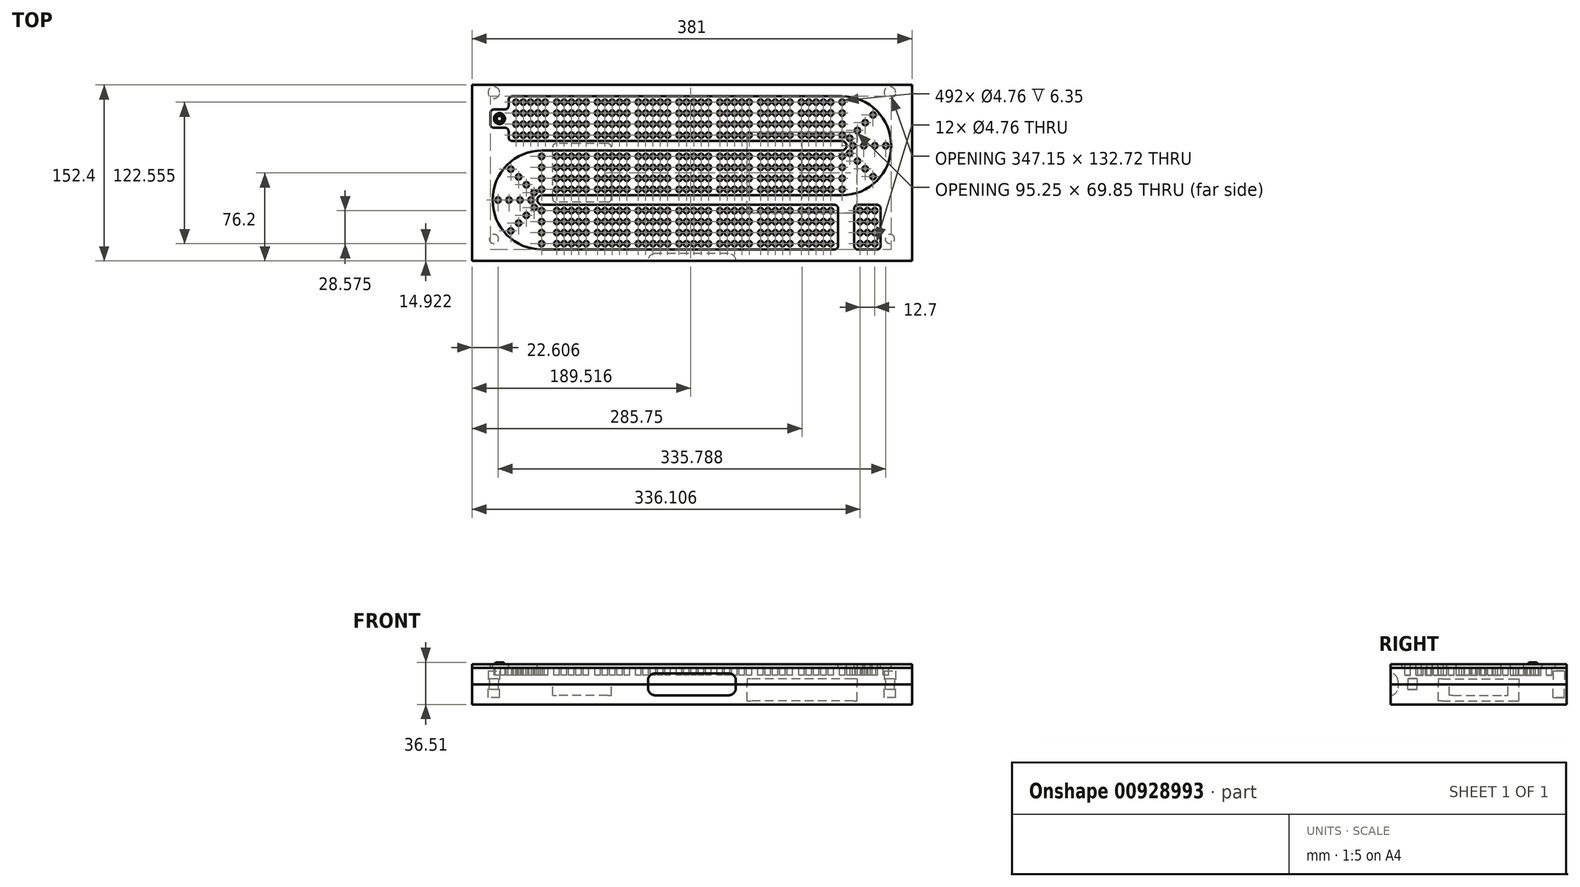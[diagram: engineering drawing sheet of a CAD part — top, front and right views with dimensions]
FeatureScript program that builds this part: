
annotation { "Feature Type Name" : "Feature", "Feature Type Description" : "" }
export const myFeature = defineFeature(function(context is Context, id is Id, definition is map)
    precondition{}
    {
        {
            var Q0;
            Q0=qCreatedBy(makeId("Top.planeOp"),FACE);
            var sketch = newSketch(context, id + "F0", { "sketchPlane" : qUnion([Q0])});
            skLineSegment(sketch, "E0.bottom", {"start": v(190.5, -76.2) * mm, "end": v(-190.5, -76.2) * mm});
            skLineSegment(sketch, "E0.top", {"start": v(190.5, 76.2) * mm, "end": v(-190.5, 76.2) * mm});
            skLineSegment(sketch, "E0.left", {"start": v(190.5, -76.2) * mm, "end": v(190.5, 76.2) * mm});
            skLineSegment(sketch, "E0.right", {"start": v(-190.5, -76.2) * mm, "end": v(-190.5, 76.2) * mm});
            skPoint(sketch, "E0.middle", {"position": v(0, 0) * mm});
            skSolve(sketch);
        }
        {
            var Q0;
            Q0=makeQuery(id+"F0.imprint","IMPRINT",FACE,{"disambiguationData":[TD([[makeQuery(id+"F0.imprint","IMPRINT",EDGE,{"derivedFrom":sQuery(id+"F0.wireOp",EDGE,"E0.bottom")}),-1.0]])]});
            extrude(context, id + "F1", {"entities" : qUnion([Q0]), "oppositeDirection" : true, "depth" : 17.46 * mm, "offsetDistance" : 25.4 * mm});
        }
        {
            var Q0;
            Q0=makeQuery(id+"F1.opExtrude","CAP_FACE",FACE,{"disambiguationData":[OSD([sQuery(id+"F0.wireOp",EDGE,"E0.bottom"),sQuery(id+"F0.wireOp",EDGE,"E0.top"),sQuery(id+"F0.wireOp",EDGE,"E0.left"),sQuery(id+"F0.wireOp",EDGE,"E0.right")])],"isStart":true});
            var sketch = newSketch(context, id + "F2", { "sketchPlane" : qUnion([Q0])});
            skCircle(sketch, "E1", {"center": v(1.59, -14.29) * mm, "radius": 2.38 * mm});
            skCircle(sketch, "E2.0.1.0", {"center": v(1.59, -4.76) * mm, "radius": 2.38 * mm});
            skCircle(sketch, "E2.0.2.0", {"center": v(1.59, 4.76) * mm, "radius": 2.38 * mm});
            skCircle(sketch, "E2.0.3.0", {"center": v(1.59, 14.29) * mm, "radius": 2.38 * mm});
            skCircle(sketch, "E2.1.0.0", {"center": v(7.94, -14.29) * mm, "radius": 2.38 * mm});
            skCircle(sketch, "E2.1.1.0", {"center": v(7.94, -4.76) * mm, "radius": 2.38 * mm});
            skCircle(sketch, "E2.1.2.0", {"center": v(7.94, 4.76) * mm, "radius": 2.38 * mm});
            skCircle(sketch, "E2.1.3.0", {"center": v(7.94, 14.29) * mm, "radius": 2.38 * mm});
            skCircle(sketch, "E2.2.0.0", {"center": v(14.29, -14.29) * mm, "radius": 2.38 * mm});
            skCircle(sketch, "E2.2.1.0", {"center": v(14.29, -4.76) * mm, "radius": 2.38 * mm});
            skCircle(sketch, "E2.2.2.0", {"center": v(14.29, 4.76) * mm, "radius": 2.38 * mm});
            skCircle(sketch, "E2.2.3.0", {"center": v(14.29, 14.29) * mm, "radius": 2.38 * mm});
            skCircle(sketch, "E3.1.0.0", {"center": v(-4.76, -14.29) * mm, "radius": 2.38 * mm});
            skCircle(sketch, "E3.2.0.0", {"center": v(-11.11, -14.29) * mm, "radius": 2.38 * mm});
            skCircle(sketch, "E4.0.1.0", {"center": v(-4.76, -4.76) * mm, "radius": 2.38 * mm});
            skCircle(sketch, "E4.0.2.0", {"center": v(-4.76, 4.76) * mm, "radius": 2.38 * mm});
            skCircle(sketch, "E4.0.3.0", {"center": v(-4.76, 14.29) * mm, "radius": 2.38 * mm});
            skCircle(sketch, "E5.0.1.0", {"center": v(-11.11, -4.76) * mm, "radius": 2.38 * mm});
            skCircle(sketch, "E5.0.2.0", {"center": v(-11.11, 4.76) * mm, "radius": 2.38 * mm});
            skCircle(sketch, "E5.0.3.0", {"center": v(-11.11, 14.29) * mm, "radius": 2.38 * mm});
            skCircle(sketch, "E6.1.0.0", {"center": v(30.54, 4.76) * mm, "radius": 2.38 * mm});
            skCircle(sketch, "E6.1.0.1", {"center": v(43.24, -14.29) * mm, "radius": 2.38 * mm});
            skCircle(sketch, "E6.1.0.2", {"center": v(43.24, -4.76) * mm, "radius": 2.38 * mm});
            skCircle(sketch, "E6.1.0.3", {"center": v(43.24, 14.29) * mm, "radius": 2.38 * mm});
            skCircle(sketch, "E6.1.0.4", {"center": v(49.6, 14.29) * mm, "radius": 2.38 * mm});
            skCircle(sketch, "E6.1.0.5", {"center": v(24.2, -14.29) * mm, "radius": 2.38 * mm});
            skCircle(sketch, "E6.1.0.6", {"center": v(30.54, -4.76) * mm, "radius": 2.38 * mm});
            skCircle(sketch, "E6.1.0.7", {"center": v(49.6, -4.76) * mm, "radius": 2.38 * mm});
            skCircle(sketch, "E6.1.0.8", {"center": v(36.9, 14.29) * mm, "radius": 2.38 * mm});
            skCircle(sketch, "E6.1.0.9", {"center": v(30.54, -14.29) * mm, "radius": 2.38 * mm});
            skCircle(sketch, "E6.1.0.10", {"center": v(24.2, -4.76) * mm, "radius": 2.38 * mm});
            skCircle(sketch, "E6.1.0.11", {"center": v(49.6, -14.29) * mm, "radius": 2.38 * mm});
            skCircle(sketch, "E6.1.0.12", {"center": v(36.9, -14.29) * mm, "radius": 2.38 * mm});
            skCircle(sketch, "E6.1.0.13", {"center": v(36.9, -4.76) * mm, "radius": 2.38 * mm});
            skCircle(sketch, "E6.1.0.14", {"center": v(30.54, 14.29) * mm, "radius": 2.38 * mm});
            skCircle(sketch, "E6.1.0.15", {"center": v(43.24, 4.76) * mm, "radius": 2.38 * mm});
            skCircle(sketch, "E6.1.0.16", {"center": v(24.2, 14.29) * mm, "radius": 2.38 * mm});
            skCircle(sketch, "E6.1.0.17", {"center": v(49.6, 4.76) * mm, "radius": 2.38 * mm});
            skCircle(sketch, "E6.1.0.18", {"center": v(24.2, 4.76) * mm, "radius": 2.38 * mm});
            skCircle(sketch, "E6.1.0.19", {"center": v(36.9, 4.76) * mm, "radius": 2.38 * mm});
            skCircle(sketch, "E6.2.0.0", {"center": v(65.85, 4.76) * mm, "radius": 2.38 * mm});
            skCircle(sketch, "E6.2.0.1", {"center": v(78.55, -14.29) * mm, "radius": 2.38 * mm});
            skCircle(sketch, "E6.2.0.2", {"center": v(78.55, -4.76) * mm, "radius": 2.38 * mm});
            skCircle(sketch, "E6.2.0.3", {"center": v(78.55, 14.29) * mm, "radius": 2.38 * mm});
            skCircle(sketch, "E6.2.0.4", {"center": v(84.9, 14.29) * mm, "radius": 2.38 * mm});
            skCircle(sketch, "E6.2.0.5", {"center": v(59.5, -14.29) * mm, "radius": 2.38 * mm});
            skCircle(sketch, "E6.2.0.6", {"center": v(65.85, -4.76) * mm, "radius": 2.38 * mm});
            skCircle(sketch, "E6.2.0.7", {"center": v(84.9, -4.76) * mm, "radius": 2.38 * mm});
            skCircle(sketch, "E6.2.0.8", {"center": v(72.2, 14.29) * mm, "radius": 2.38 * mm});
            skCircle(sketch, "E6.2.0.9", {"center": v(65.85, -14.29) * mm, "radius": 2.38 * mm});
            skCircle(sketch, "E6.2.0.10", {"center": v(59.5, -4.76) * mm, "radius": 2.38 * mm});
            skCircle(sketch, "E6.2.0.11", {"center": v(84.9, -14.29) * mm, "radius": 2.38 * mm});
            skCircle(sketch, "E6.2.0.12", {"center": v(72.2, -14.29) * mm, "radius": 2.38 * mm});
            skCircle(sketch, "E6.2.0.13", {"center": v(72.2, -4.76) * mm, "radius": 2.38 * mm});
            skCircle(sketch, "E6.2.0.14", {"center": v(65.85, 14.29) * mm, "radius": 2.38 * mm});
            skCircle(sketch, "E6.2.0.15", {"center": v(78.55, 4.76) * mm, "radius": 2.38 * mm});
            skCircle(sketch, "E6.2.0.16", {"center": v(59.5, 14.29) * mm, "radius": 2.38 * mm});
            skCircle(sketch, "E6.2.0.17", {"center": v(84.9, 4.76) * mm, "radius": 2.38 * mm});
            skCircle(sketch, "E6.2.0.18", {"center": v(59.5, 4.76) * mm, "radius": 2.38 * mm});
            skCircle(sketch, "E6.2.0.19", {"center": v(72.2, 4.76) * mm, "radius": 2.38 * mm});
            skCircle(sketch, "E6.3.0.0", {"center": v(101.16, 4.76) * mm, "radius": 2.38 * mm});
            skCircle(sketch, "E6.3.0.1", {"center": v(113.86, -14.29) * mm, "radius": 2.38 * mm});
            skCircle(sketch, "E6.3.0.2", {"center": v(113.86, -4.76) * mm, "radius": 2.38 * mm});
            skCircle(sketch, "E6.3.0.3", {"center": v(113.86, 14.29) * mm, "radius": 2.38 * mm});
            skCircle(sketch, "E6.3.0.4", {"center": v(120.2, 14.29) * mm, "radius": 2.38 * mm});
            skCircle(sketch, "E6.3.0.5", {"center": v(94.8, -14.29) * mm, "radius": 2.38 * mm});
            skCircle(sketch, "E6.3.0.6", {"center": v(101.16, -4.76) * mm, "radius": 2.38 * mm});
            skCircle(sketch, "E6.3.0.7", {"center": v(120.2, -4.76) * mm, "radius": 2.38 * mm});
            skCircle(sketch, "E6.3.0.8", {"center": v(107.5, 14.29) * mm, "radius": 2.38 * mm});
            skCircle(sketch, "E6.3.0.9", {"center": v(101.16, -14.29) * mm, "radius": 2.38 * mm});
            skCircle(sketch, "E6.3.0.10", {"center": v(94.8, -4.76) * mm, "radius": 2.38 * mm});
            skCircle(sketch, "E6.3.0.11", {"center": v(120.2, -14.29) * mm, "radius": 2.38 * mm});
            skCircle(sketch, "E6.3.0.12", {"center": v(107.5, -14.29) * mm, "radius": 2.38 * mm});
            skCircle(sketch, "E6.3.0.13", {"center": v(107.5, -4.76) * mm, "radius": 2.38 * mm});
            skCircle(sketch, "E6.3.0.14", {"center": v(101.16, 14.29) * mm, "radius": 2.38 * mm});
            skCircle(sketch, "E6.3.0.15", {"center": v(113.86, 4.76) * mm, "radius": 2.38 * mm});
            skCircle(sketch, "E6.3.0.16", {"center": v(94.8, 14.29) * mm, "radius": 2.38 * mm});
            skCircle(sketch, "E6.3.0.17", {"center": v(120.2, 4.76) * mm, "radius": 2.38 * mm});
            skCircle(sketch, "E6.3.0.18", {"center": v(94.8, 4.76) * mm, "radius": 2.38 * mm});
            skCircle(sketch, "E6.3.0.19", {"center": v(107.5, 4.76) * mm, "radius": 2.38 * mm});
            skLineSegment(sketch, "E6.direction1", {"start": v(-11.11, -14.29) * mm, "end": v(24.2, -14.29) * mm, "construction": true});
            skCircle(sketch, "E7.1.0.0", {"center": v(-46.42, 4.76) * mm, "radius": 2.38 * mm});
            skCircle(sketch, "E7.1.0.1", {"center": v(-46.42, -14.29) * mm, "radius": 2.38 * mm});
            skCircle(sketch, "E7.1.0.2", {"center": v(-21.02, 14.29) * mm, "radius": 2.38 * mm});
            skCircle(sketch, "E7.1.0.3", {"center": v(-33.72, 4.76) * mm, "radius": 2.38 * mm});
            skCircle(sketch, "E7.1.0.4", {"center": v(-46.42, 14.29) * mm, "radius": 2.38 * mm});
            skCircle(sketch, "E7.1.0.5", {"center": v(-33.72, -14.29) * mm, "radius": 2.38 * mm});
            skCircle(sketch, "E7.1.0.6", {"center": v(-33.72, -4.76) * mm, "radius": 2.38 * mm});
            skCircle(sketch, "E7.1.0.7", {"center": v(-46.42, -4.76) * mm, "radius": 2.38 * mm});
            skCircle(sketch, "E7.1.0.8", {"center": v(-27.37, -4.76) * mm, "radius": 2.38 * mm});
            skCircle(sketch, "E7.1.0.9", {"center": v(-40.07, -4.76) * mm, "radius": 2.38 * mm});
            skCircle(sketch, "E7.1.0.10", {"center": v(-27.37, 4.76) * mm, "radius": 2.38 * mm});
            skCircle(sketch, "E7.1.0.11", {"center": v(-21.02, -4.76) * mm, "radius": 2.38 * mm});
            skCircle(sketch, "E7.1.0.12", {"center": v(-40.07, 14.29) * mm, "radius": 2.38 * mm});
            skCircle(sketch, "E7.1.0.13", {"center": v(-21.02, 4.76) * mm, "radius": 2.38 * mm});
            skCircle(sketch, "E7.1.0.14", {"center": v(-40.07, 4.76) * mm, "radius": 2.38 * mm});
            skCircle(sketch, "E7.1.0.15", {"center": v(-33.72, 14.29) * mm, "radius": 2.38 * mm});
            skCircle(sketch, "E7.1.0.16", {"center": v(-27.37, -14.29) * mm, "radius": 2.38 * mm});
            skCircle(sketch, "E7.1.0.17", {"center": v(-27.37, 14.29) * mm, "radius": 2.38 * mm});
            skCircle(sketch, "E7.1.0.18", {"center": v(-40.07, -14.29) * mm, "radius": 2.38 * mm});
            skCircle(sketch, "E7.1.0.19", {"center": v(-21.02, -14.29) * mm, "radius": 2.38 * mm});
            skCircle(sketch, "E7.2.0.0", {"center": v(-81.72, 4.76) * mm, "radius": 2.38 * mm});
            skCircle(sketch, "E7.2.0.1", {"center": v(-81.72, -14.29) * mm, "radius": 2.38 * mm});
            skCircle(sketch, "E7.2.0.2", {"center": v(-56.32, 14.29) * mm, "radius": 2.38 * mm});
            skCircle(sketch, "E7.2.0.3", {"center": v(-69.02, 4.76) * mm, "radius": 2.38 * mm});
            skCircle(sketch, "E7.2.0.4", {"center": v(-81.72, 14.29) * mm, "radius": 2.38 * mm});
            skCircle(sketch, "E7.2.0.5", {"center": v(-69.02, -14.29) * mm, "radius": 2.38 * mm});
            skCircle(sketch, "E7.2.0.6", {"center": v(-69.02, -4.76) * mm, "radius": 2.38 * mm});
            skCircle(sketch, "E7.2.0.7", {"center": v(-81.72, -4.76) * mm, "radius": 2.38 * mm});
            skCircle(sketch, "E7.2.0.8", {"center": v(-62.67, -4.76) * mm, "radius": 2.38 * mm});
            skCircle(sketch, "E7.2.0.9", {"center": v(-75.37, -4.76) * mm, "radius": 2.38 * mm});
            skCircle(sketch, "E7.2.0.10", {"center": v(-62.67, 4.76) * mm, "radius": 2.38 * mm});
            skCircle(sketch, "E7.2.0.11", {"center": v(-56.32, -4.76) * mm, "radius": 2.38 * mm});
            skCircle(sketch, "E7.2.0.12", {"center": v(-75.37, 14.29) * mm, "radius": 2.38 * mm});
            skCircle(sketch, "E7.2.0.13", {"center": v(-56.32, 4.76) * mm, "radius": 2.38 * mm});
            skCircle(sketch, "E7.2.0.14", {"center": v(-75.37, 4.76) * mm, "radius": 2.38 * mm});
            skCircle(sketch, "E7.2.0.15", {"center": v(-69.02, 14.29) * mm, "radius": 2.38 * mm});
            skCircle(sketch, "E7.2.0.16", {"center": v(-62.67, -14.29) * mm, "radius": 2.38 * mm});
            skCircle(sketch, "E7.2.0.17", {"center": v(-62.67, 14.29) * mm, "radius": 2.38 * mm});
            skCircle(sketch, "E7.2.0.18", {"center": v(-75.37, -14.29) * mm, "radius": 2.38 * mm});
            skCircle(sketch, "E7.2.0.19", {"center": v(-56.32, -14.29) * mm, "radius": 2.38 * mm});
            skCircle(sketch, "E7.3.0.0", {"center": v(-117.03, 4.76) * mm, "radius": 2.38 * mm});
            skCircle(sketch, "E7.3.0.1", {"center": v(-117.03, -14.29) * mm, "radius": 2.38 * mm});
            skCircle(sketch, "E7.3.0.2", {"center": v(-91.63, 14.29) * mm, "radius": 2.38 * mm});
            skCircle(sketch, "E7.3.0.3", {"center": v(-104.33, 4.76) * mm, "radius": 2.38 * mm});
            skCircle(sketch, "E7.3.0.4", {"center": v(-117.03, 14.29) * mm, "radius": 2.38 * mm});
            skCircle(sketch, "E7.3.0.5", {"center": v(-104.33, -14.29) * mm, "radius": 2.38 * mm});
            skCircle(sketch, "E7.3.0.6", {"center": v(-104.33, -4.76) * mm, "radius": 2.38 * mm});
            skCircle(sketch, "E7.3.0.7", {"center": v(-117.03, -4.76) * mm, "radius": 2.38 * mm});
            skCircle(sketch, "E7.3.0.8", {"center": v(-97.98, -4.76) * mm, "radius": 2.38 * mm});
            skCircle(sketch, "E7.3.0.9", {"center": v(-110.68, -4.76) * mm, "radius": 2.38 * mm});
            skCircle(sketch, "E7.3.0.10", {"center": v(-97.98, 4.76) * mm, "radius": 2.38 * mm});
            skCircle(sketch, "E7.3.0.11", {"center": v(-91.63, -4.76) * mm, "radius": 2.38 * mm});
            skCircle(sketch, "E7.3.0.12", {"center": v(-110.68, 14.29) * mm, "radius": 2.38 * mm});
            skCircle(sketch, "E7.3.0.13", {"center": v(-91.63, 4.76) * mm, "radius": 2.38 * mm});
            skCircle(sketch, "E7.3.0.14", {"center": v(-110.68, 4.76) * mm, "radius": 2.38 * mm});
            skCircle(sketch, "E7.3.0.15", {"center": v(-104.33, 14.29) * mm, "radius": 2.38 * mm});
            skCircle(sketch, "E7.3.0.16", {"center": v(-97.98, -14.29) * mm, "radius": 2.38 * mm});
            skCircle(sketch, "E7.3.0.17", {"center": v(-97.98, 14.29) * mm, "radius": 2.38 * mm});
            skCircle(sketch, "E7.3.0.18", {"center": v(-110.68, -14.29) * mm, "radius": 2.38 * mm});
            skCircle(sketch, "E7.3.0.19", {"center": v(-91.63, -14.29) * mm, "radius": 2.38 * mm});
            skCircle(sketch, "E8.0.1.0", {"center": v(94.8, 61.28) * mm, "radius": 2.38 * mm});
            skCircle(sketch, "E8.0.1.1", {"center": v(-81.72, 32.7) * mm, "radius": 2.38 * mm});
            skCircle(sketch, "E8.0.1.2", {"center": v(1.59, 61.28) * mm, "radius": 2.38 * mm});
            skCircle(sketch, "E8.0.1.3", {"center": v(49.6, 51.75) * mm, "radius": 2.38 * mm});
            skCircle(sketch, "E8.0.1.4", {"center": v(-40.07, 32.7) * mm, "radius": 2.38 * mm});
            skCircle(sketch, "E8.0.1.5", {"center": v(-104.33, 42.23) * mm, "radius": 2.38 * mm});
            skCircle(sketch, "E8.0.1.6", {"center": v(36.9, 32.7) * mm, "radius": 2.38 * mm});
            skCircle(sketch, "E8.0.1.7", {"center": v(49.6, 42.23) * mm, "radius": 2.38 * mm});
            skCircle(sketch, "E8.0.1.8", {"center": v(24.2, 42.23) * mm, "radius": 2.38 * mm});
            skCircle(sketch, "E8.0.1.9", {"center": v(-110.68, 61.28) * mm, "radius": 2.38 * mm});
            skCircle(sketch, "E8.0.1.10", {"center": v(1.59, 42.23) * mm, "radius": 2.38 * mm});
            skCircle(sketch, "E8.0.1.11", {"center": v(78.55, 42.23) * mm, "radius": 2.38 * mm});
            skCircle(sketch, "E8.0.1.12", {"center": v(-69.02, 42.23) * mm, "radius": 2.38 * mm});
            skCircle(sketch, "E8.0.1.13", {"center": v(65.85, 61.28) * mm, "radius": 2.38 * mm});
            skCircle(sketch, "E8.0.1.14", {"center": v(-33.72, 42.23) * mm, "radius": 2.38 * mm});
            skCircle(sketch, "E8.0.1.15", {"center": v(-81.72, 42.23) * mm, "radius": 2.38 * mm});
            skCircle(sketch, "E8.0.1.16", {"center": v(78.55, 32.7) * mm, "radius": 2.38 * mm});
            skCircle(sketch, "E8.0.1.17", {"center": v(-117.03, 32.7) * mm, "radius": 2.38 * mm});
            skCircle(sketch, "E8.0.1.18", {"center": v(36.9, 42.23) * mm, "radius": 2.38 * mm});
            skCircle(sketch, "E8.0.1.19", {"center": v(-97.98, 51.75) * mm, "radius": 2.38 * mm});
            skCircle(sketch, "E8.0.1.20", {"center": v(107.5, 61.28) * mm, "radius": 2.38 * mm});
            skCircle(sketch, "E8.0.1.21", {"center": v(101.16, 61.28) * mm, "radius": 2.38 * mm});
            skCircle(sketch, "E8.0.1.22", {"center": v(72.2, 42.23) * mm, "radius": 2.38 * mm});
            skCircle(sketch, "E8.0.1.23", {"center": v(30.54, 51.75) * mm, "radius": 2.38 * mm});
            skCircle(sketch, "E8.0.1.24", {"center": v(94.8, 51.75) * mm, "radius": 2.38 * mm});
            skCircle(sketch, "E8.0.1.25", {"center": v(49.6, 32.7) * mm, "radius": 2.38 * mm});
            skCircle(sketch, "E8.0.1.26", {"center": v(-27.37, 61.28) * mm, "radius": 2.38 * mm});
            skCircle(sketch, "E8.0.1.27", {"center": v(-69.02, 61.28) * mm, "radius": 2.38 * mm});
            skCircle(sketch, "E8.0.1.28", {"center": v(-110.68, 42.23) * mm, "radius": 2.38 * mm});
            skCircle(sketch, "E8.0.1.29", {"center": v(-97.98, 32.7) * mm, "radius": 2.38 * mm});
            skCircle(sketch, "E8.0.1.30", {"center": v(7.94, 61.28) * mm, "radius": 2.38 * mm});
            skCircle(sketch, "E8.0.1.31", {"center": v(14.29, 61.28) * mm, "radius": 2.38 * mm});
            skCircle(sketch, "E8.0.1.32", {"center": v(-21.02, 51.75) * mm, "radius": 2.38 * mm});
            skCircle(sketch, "E8.0.1.33", {"center": v(101.16, 42.23) * mm, "radius": 2.38 * mm});
            skCircle(sketch, "E8.0.1.35", {"center": v(65.85, 51.75) * mm, "radius": 2.38 * mm});
            skCircle(sketch, "E8.0.1.36", {"center": v(7.94, 42.23) * mm, "radius": 2.38 * mm});
            skCircle(sketch, "E8.0.1.37", {"center": v(59.5, 61.28) * mm, "radius": 2.38 * mm});
            skCircle(sketch, "E8.0.1.38", {"center": v(-62.67, 32.7) * mm, "radius": 2.38 * mm});
            skCircle(sketch, "E8.0.1.39", {"center": v(-117.03, 42.23) * mm, "radius": 2.38 * mm});
            skCircle(sketch, "E8.0.1.40", {"center": v(-11.11, 61.28) * mm, "radius": 2.38 * mm});
            skCircle(sketch, "E8.0.1.41", {"center": v(-81.72, 51.75) * mm, "radius": 2.38 * mm});
            skCircle(sketch, "E8.0.1.42", {"center": v(113.86, 61.28) * mm, "radius": 2.38 * mm});
            skCircle(sketch, "E8.0.1.43", {"center": v(-69.02, 32.7) * mm, "radius": 2.38 * mm});
            skCircle(sketch, "E8.0.1.44", {"center": v(-27.37, 51.75) * mm, "radius": 2.38 * mm});
            skCircle(sketch, "E8.0.1.45", {"center": v(30.54, 61.28) * mm, "radius": 2.38 * mm});
            skCircle(sketch, "E8.0.1.46", {"center": v(14.29, 42.23) * mm, "radius": 2.38 * mm});
            skCircle(sketch, "E8.0.1.47", {"center": v(-11.11, 51.75) * mm, "radius": 2.38 * mm});
            skCircle(sketch, "E8.0.1.48", {"center": v(-40.07, 42.23) * mm, "radius": 2.38 * mm});
            skCircle(sketch, "E8.0.1.49", {"center": v(65.85, 32.7) * mm, "radius": 2.38 * mm});
            skCircle(sketch, "E8.0.1.50", {"center": v(24.2, 61.28) * mm, "radius": 2.38 * mm});
            skCircle(sketch, "E8.0.1.51", {"center": v(78.55, 61.28) * mm, "radius": 2.38 * mm});
            skCircle(sketch, "E8.0.1.52", {"center": v(-97.98, 42.23) * mm, "radius": 2.38 * mm});
            skCircle(sketch, "E8.0.1.53", {"center": v(94.8, 32.7) * mm, "radius": 2.38 * mm});
            skCircle(sketch, "E8.0.1.54", {"center": v(120.2, 61.28) * mm, "radius": 2.38 * mm});
            skCircle(sketch, "E8.0.1.55", {"center": v(-11.11, 42.23) * mm, "radius": 2.38 * mm});
            skCircle(sketch, "E8.0.1.56", {"center": v(-40.07, 61.28) * mm, "radius": 2.38 * mm});
            skCircle(sketch, "E8.0.1.57", {"center": v(-91.63, 51.75) * mm, "radius": 2.38 * mm});
            skCircle(sketch, "E8.0.1.58", {"center": v(7.94, 51.75) * mm, "radius": 2.38 * mm});
            skCircle(sketch, "E8.0.1.59", {"center": v(120.2, 42.23) * mm, "radius": 2.38 * mm});
            skCircle(sketch, "E8.0.1.60", {"center": v(94.8, 42.23) * mm, "radius": 2.38 * mm});
            skCircle(sketch, "E8.0.1.61", {"center": v(113.86, 42.23) * mm, "radius": 2.38 * mm});
            skCircle(sketch, "E8.0.1.62", {"center": v(-56.32, 51.75) * mm, "radius": 2.38 * mm});
            skCircle(sketch, "E8.0.1.63", {"center": v(-75.37, 61.28) * mm, "radius": 2.38 * mm});
            skCircle(sketch, "E8.0.1.64", {"center": v(-11.11, 32.7) * mm, "radius": 2.38 * mm});
            skCircle(sketch, "E8.0.1.65", {"center": v(84.9, 61.28) * mm, "radius": 2.38 * mm});
            skCircle(sketch, "E8.0.1.66", {"center": v(-91.63, 61.28) * mm, "radius": 2.38 * mm});
            skCircle(sketch, "E8.0.1.67", {"center": v(-56.32, 32.7) * mm, "radius": 2.38 * mm});
            skCircle(sketch, "E8.0.1.68", {"center": v(-97.98, 61.28) * mm, "radius": 2.38 * mm});
            skCircle(sketch, "E8.0.1.69", {"center": v(43.24, 61.28) * mm, "radius": 2.38 * mm});
            skCircle(sketch, "E8.0.1.70", {"center": v(-81.72, 61.28) * mm, "radius": 2.38 * mm});
            skCircle(sketch, "E8.0.1.71", {"center": v(59.5, 42.23) * mm, "radius": 2.38 * mm});
            skCircle(sketch, "E8.0.1.72", {"center": v(-27.37, 42.23) * mm, "radius": 2.38 * mm});
            skCircle(sketch, "E8.0.1.73", {"center": v(107.5, 32.7) * mm, "radius": 2.38 * mm});
            skCircle(sketch, "E8.0.1.74", {"center": v(-4.76, 42.23) * mm, "radius": 2.38 * mm});
            skCircle(sketch, "E8.0.1.75", {"center": v(-33.72, 61.28) * mm, "radius": 2.38 * mm});
            skCircle(sketch, "E8.0.1.76", {"center": v(-104.33, 61.28) * mm, "radius": 2.38 * mm});
            skCircle(sketch, "E8.0.1.77", {"center": v(84.9, 51.75) * mm, "radius": 2.38 * mm});
            skCircle(sketch, "E8.0.1.78", {"center": v(43.24, 42.23) * mm, "radius": 2.38 * mm});
            skCircle(sketch, "E8.0.1.79", {"center": v(-91.63, 42.23) * mm, "radius": 2.38 * mm});
            skCircle(sketch, "E8.0.1.80", {"center": v(30.54, 42.23) * mm, "radius": 2.38 * mm});
            skCircle(sketch, "E8.0.1.81", {"center": v(49.6, 61.28) * mm, "radius": 2.38 * mm});
            skCircle(sketch, "E8.0.1.82", {"center": v(36.9, 61.28) * mm, "radius": 2.38 * mm});
            skCircle(sketch, "E8.0.1.83", {"center": v(-75.37, 42.23) * mm, "radius": 2.38 * mm});
            skCircle(sketch, "E8.0.1.84", {"center": v(-91.63, 32.7) * mm, "radius": 2.38 * mm});
            skCircle(sketch, "E8.0.1.85", {"center": v(65.85, 42.23) * mm, "radius": 2.38 * mm});
            skCircle(sketch, "E8.0.1.86", {"center": v(-56.32, 42.23) * mm, "radius": 2.38 * mm});
            skCircle(sketch, "E8.0.1.87", {"center": v(-46.42, 61.28) * mm, "radius": 2.38 * mm});
            skCircle(sketch, "E8.0.1.88", {"center": v(-40.07, 51.75) * mm, "radius": 2.38 * mm});
            skCircle(sketch, "E8.0.1.89", {"center": v(-27.37, 32.7) * mm, "radius": 2.38 * mm});
            skCircle(sketch, "E8.0.1.90", {"center": v(84.9, 42.23) * mm, "radius": 2.38 * mm});
            skCircle(sketch, "E8.0.1.91", {"center": v(-21.02, 42.23) * mm, "radius": 2.38 * mm});
            skCircle(sketch, "E8.0.1.92", {"center": v(-62.67, 61.28) * mm, "radius": 2.38 * mm});
            skCircle(sketch, "E8.0.1.93", {"center": v(-56.32, 61.28) * mm, "radius": 2.38 * mm});
            skCircle(sketch, "E8.0.1.94", {"center": v(72.2, 61.28) * mm, "radius": 2.38 * mm});
            skCircle(sketch, "E8.0.1.95", {"center": v(-117.03, 51.75) * mm, "radius": 2.38 * mm});
            skCircle(sketch, "E8.0.1.96", {"center": v(113.86, 51.75) * mm, "radius": 2.38 * mm});
            skCircle(sketch, "E8.0.1.97", {"center": v(-62.67, 51.75) * mm, "radius": 2.38 * mm});
            skCircle(sketch, "E8.0.1.98", {"center": v(-4.76, 61.28) * mm, "radius": 2.38 * mm});
            skCircle(sketch, "E8.0.1.99", {"center": v(-62.67, 42.23) * mm, "radius": 2.38 * mm});
            skCircle(sketch, "E8.0.1.100", {"center": v(-69.02, 51.75) * mm, "radius": 2.38 * mm});
            skCircle(sketch, "E8.0.1.101", {"center": v(-21.02, 61.28) * mm, "radius": 2.38 * mm});
            skCircle(sketch, "E8.0.1.102", {"center": v(107.5, 42.23) * mm, "radius": 2.38 * mm});
            skCircle(sketch, "E8.0.1.103", {"center": v(-46.42, 42.23) * mm, "radius": 2.38 * mm});
            skCircle(sketch, "E8.0.1.104", {"center": v(-117.03, 61.28) * mm, "radius": 2.38 * mm});
            skCircle(sketch, "E8.0.1.105", {"center": v(59.5, 32.7) * mm, "radius": 2.38 * mm});
            skCircle(sketch, "E8.0.1.106", {"center": v(1.59, 32.7) * mm, "radius": 2.38 * mm});
            skCircle(sketch, "E8.0.1.107", {"center": v(1.59, 51.75) * mm, "radius": 2.38 * mm});
            skCircle(sketch, "E8.0.1.108", {"center": v(-110.68, 51.75) * mm, "radius": 2.38 * mm});
            skCircle(sketch, "E8.0.1.109", {"center": v(-75.37, 51.75) * mm, "radius": 2.38 * mm});
            skCircle(sketch, "E8.0.1.110", {"center": v(-4.76, 51.75) * mm, "radius": 2.38 * mm});
            skCircle(sketch, "E8.0.1.111", {"center": v(120.2, 32.7) * mm, "radius": 2.38 * mm});
            skCircle(sketch, "E8.0.1.112", {"center": v(-110.68, 32.7) * mm, "radius": 2.38 * mm});
            skCircle(sketch, "E8.0.1.113", {"center": v(84.9, 32.7) * mm, "radius": 2.38 * mm});
            skCircle(sketch, "E8.0.1.114", {"center": v(-46.42, 51.75) * mm, "radius": 2.38 * mm});
            skCircle(sketch, "E8.0.1.115", {"center": v(-4.76, 32.7) * mm, "radius": 2.38 * mm});
            skCircle(sketch, "E8.0.1.116", {"center": v(101.16, 32.7) * mm, "radius": 2.38 * mm});
            skCircle(sketch, "E8.0.1.117", {"center": v(-21.02, 32.7) * mm, "radius": 2.38 * mm});
            skCircle(sketch, "E8.0.1.118", {"center": v(-104.33, 51.75) * mm, "radius": 2.38 * mm});
            skCircle(sketch, "E8.0.1.119", {"center": v(7.94, 32.7) * mm, "radius": 2.38 * mm});
            skCircle(sketch, "E8.0.1.120", {"center": v(30.54, 32.7) * mm, "radius": 2.38 * mm});
            skCircle(sketch, "E8.0.1.121", {"center": v(59.5, 51.75) * mm, "radius": 2.38 * mm});
            skCircle(sketch, "E8.0.1.122", {"center": v(113.86, 32.7) * mm, "radius": 2.38 * mm});
            skCircle(sketch, "E8.0.1.123", {"center": v(120.2, 51.75) * mm, "radius": 2.38 * mm});
            skCircle(sketch, "E8.0.1.124", {"center": v(-104.33, 32.7) * mm, "radius": 2.38 * mm});
            skCircle(sketch, "E8.0.1.125", {"center": v(72.2, 32.7) * mm, "radius": 2.38 * mm});
            skCircle(sketch, "E8.0.1.126", {"center": v(14.29, 32.7) * mm, "radius": 2.38 * mm});
            skCircle(sketch, "E8.0.1.127", {"center": v(24.2, 51.75) * mm, "radius": 2.38 * mm});
            skCircle(sketch, "E8.0.1.128", {"center": v(-33.72, 32.7) * mm, "radius": 2.38 * mm});
            skCircle(sketch, "E8.0.1.129", {"center": v(107.5, 51.75) * mm, "radius": 2.38 * mm});
            skCircle(sketch, "E8.0.1.130", {"center": v(-75.37, 32.7) * mm, "radius": 2.38 * mm});
            skCircle(sketch, "E8.0.1.131", {"center": v(-33.72, 51.75) * mm, "radius": 2.38 * mm});
            skCircle(sketch, "E8.0.1.132", {"center": v(43.24, 51.75) * mm, "radius": 2.38 * mm});
            skCircle(sketch, "E8.0.1.133", {"center": v(101.16, 51.75) * mm, "radius": 2.38 * mm});
            skCircle(sketch, "E8.0.1.134", {"center": v(72.2, 51.75) * mm, "radius": 2.38 * mm});
            skCircle(sketch, "E8.0.1.135", {"center": v(-46.42, 32.7) * mm, "radius": 2.38 * mm});
            skCircle(sketch, "E8.0.1.136", {"center": v(14.29, 51.75) * mm, "radius": 2.38 * mm});
            skCircle(sketch, "E8.0.1.137", {"center": v(36.9, 51.75) * mm, "radius": 2.38 * mm});
            skCircle(sketch, "E8.0.1.138", {"center": v(43.24, 32.7) * mm, "radius": 2.38 * mm});
            skCircle(sketch, "E8.0.1.139", {"center": v(78.55, 51.75) * mm, "radius": 2.38 * mm});
            skCircle(sketch, "E8.0.1.140", {"center": v(24.2, 32.7) * mm, "radius": 2.38 * mm});
            skCircle(sketch, "E9.0.1.0", {"center": v(-75.37, -61.28) * mm, "radius": 2.38 * mm});
            skCircle(sketch, "E9.0.1.1", {"center": v(72.2, -42.23) * mm, "radius": 2.38 * mm});
            skCircle(sketch, "E9.0.1.2", {"center": v(-81.72, -51.75) * mm, "radius": 2.38 * mm});
            skCircle(sketch, "E9.0.1.3", {"center": v(7.94, -32.7) * mm, "radius": 2.38 * mm});
            skCircle(sketch, "E9.0.1.4", {"center": v(-110.68, -61.28) * mm, "radius": 2.38 * mm});
            skCircle(sketch, "E9.0.1.5", {"center": v(94.8, -51.75) * mm, "radius": 2.38 * mm});
            skCircle(sketch, "E9.0.1.7", {"center": v(49.6, -51.75) * mm, "radius": 2.38 * mm});
            skCircle(sketch, "E9.0.1.8", {"center": v(-46.42, -51.75) * mm, "radius": 2.38 * mm});
            skCircle(sketch, "E9.0.1.9", {"center": v(-97.98, -51.75) * mm, "radius": 2.38 * mm});
            skCircle(sketch, "E9.0.1.10", {"center": v(30.54, -32.7) * mm, "radius": 2.38 * mm});
            skCircle(sketch, "E9.0.1.11", {"center": v(-21.02, -32.7) * mm, "radius": 2.38 * mm});
            skCircle(sketch, "E9.0.1.12", {"center": v(-91.63, -61.28) * mm, "radius": 2.38 * mm});
            skCircle(sketch, "E9.0.1.13", {"center": v(-91.63, -51.75) * mm, "radius": 2.38 * mm});
            skCircle(sketch, "E9.0.1.14", {"center": v(59.5, -51.75) * mm, "radius": 2.38 * mm});
            skCircle(sketch, "E9.0.1.15", {"center": v(-11.11, -61.28) * mm, "radius": 2.38 * mm});
            skCircle(sketch, "E9.0.1.16", {"center": v(7.94, -51.75) * mm, "radius": 2.38 * mm});
            skCircle(sketch, "E9.0.1.17", {"center": v(-56.32, -32.7) * mm, "radius": 2.38 * mm});
            skCircle(sketch, "E9.0.1.18", {"center": v(78.55, -32.7) * mm, "radius": 2.38 * mm});
            skCircle(sketch, "E9.0.1.19", {"center": v(43.24, -61.28) * mm, "radius": 2.38 * mm});
            skCircle(sketch, "E9.0.1.20", {"center": v(-91.63, -32.7) * mm, "radius": 2.38 * mm});
            skCircle(sketch, "E9.0.1.21", {"center": v(30.54, -61.28) * mm, "radius": 2.38 * mm});
            skCircle(sketch, "E9.0.1.22", {"center": v(43.24, -51.75) * mm, "radius": 2.38 * mm});
            skCircle(sketch, "E9.0.1.23", {"center": v(36.9, -42.23) * mm, "radius": 2.38 * mm});
            skCircle(sketch, "E9.0.1.24", {"center": v(-40.07, -42.23) * mm, "radius": 2.38 * mm});
            skCircle(sketch, "E9.0.1.25", {"center": v(-69.02, -61.28) * mm, "radius": 2.38 * mm});
            skCircle(sketch, "E9.0.1.26", {"center": v(14.29, -32.7) * mm, "radius": 2.38 * mm});
            skCircle(sketch, "E9.0.1.27", {"center": v(-62.67, -51.75) * mm, "radius": 2.38 * mm});
            skCircle(sketch, "E9.0.1.28", {"center": v(120.2, -42.23) * mm, "radius": 2.38 * mm});
            skCircle(sketch, "E9.0.1.29", {"center": v(113.86, -51.75) * mm, "radius": 2.38 * mm});
            skCircle(sketch, "E9.0.1.30", {"center": v(120.2, -61.28) * mm, "radius": 2.38 * mm});
            skCircle(sketch, "E9.0.1.31", {"center": v(94.8, -32.7) * mm, "radius": 2.38 * mm});
            skCircle(sketch, "E9.0.1.32", {"center": v(78.55, -51.75) * mm, "radius": 2.38 * mm});
            skCircle(sketch, "E9.0.1.33", {"center": v(30.54, -51.75) * mm, "radius": 2.38 * mm});
            skCircle(sketch, "E9.0.1.34", {"center": v(7.94, -61.28) * mm, "radius": 2.38 * mm});
            skCircle(sketch, "E9.0.1.35", {"center": v(-110.68, -32.7) * mm, "radius": 2.38 * mm});
            skCircle(sketch, "E9.0.1.36", {"center": v(-62.67, -61.28) * mm, "radius": 2.38 * mm});
            skCircle(sketch, "E9.0.1.37", {"center": v(-104.33, -51.75) * mm, "radius": 2.38 * mm});
            skCircle(sketch, "E9.0.1.38", {"center": v(-56.32, -51.75) * mm, "radius": 2.38 * mm});
            skCircle(sketch, "E9.0.1.39", {"center": v(49.6, -32.7) * mm, "radius": 2.38 * mm});
            skCircle(sketch, "E9.0.1.40", {"center": v(120.2, -51.75) * mm, "radius": 2.38 * mm});
            skCircle(sketch, "E9.0.1.41", {"center": v(-97.98, -61.28) * mm, "radius": 2.38 * mm});
            skCircle(sketch, "E9.0.1.42", {"center": v(7.94, -42.23) * mm, "radius": 2.38 * mm});
            skCircle(sketch, "E9.0.1.43", {"center": v(-27.37, -51.75) * mm, "radius": 2.38 * mm});
            skCircle(sketch, "E9.0.1.44", {"center": v(-104.33, -32.7) * mm, "radius": 2.38 * mm});
            skCircle(sketch, "E9.0.1.45", {"center": v(107.5, -51.75) * mm, "radius": 2.38 * mm});
            skCircle(sketch, "E9.0.1.46", {"center": v(-4.76, -32.7) * mm, "radius": 2.38 * mm});
            skCircle(sketch, "E9.0.1.47", {"center": v(101.16, -61.28) * mm, "radius": 2.38 * mm});
            skCircle(sketch, "E9.0.1.48", {"center": v(1.59, -51.75) * mm, "radius": 2.38 * mm});
            skCircle(sketch, "E9.0.1.49", {"center": v(-11.11, -51.75) * mm, "radius": 2.38 * mm});
            skCircle(sketch, "E9.0.1.50", {"center": v(-117.03, -61.28) * mm, "radius": 2.38 * mm});
            skCircle(sketch, "E9.0.1.51", {"center": v(-69.02, -51.75) * mm, "radius": 2.38 * mm});
            skCircle(sketch, "E9.0.1.52", {"center": v(-91.63, -42.23) * mm, "radius": 2.38 * mm});
            skCircle(sketch, "E9.0.1.53", {"center": v(65.85, -61.28) * mm, "radius": 2.38 * mm});
            skCircle(sketch, "E9.0.1.54", {"center": v(-21.02, -61.28) * mm, "radius": 2.38 * mm});
            skCircle(sketch, "E9.0.1.55", {"center": v(-69.02, -42.23) * mm, "radius": 2.38 * mm});
            skCircle(sketch, "E9.0.1.56", {"center": v(-40.07, -51.75) * mm, "radius": 2.38 * mm});
            skCircle(sketch, "E9.0.1.57", {"center": v(-21.02, -51.75) * mm, "radius": 2.38 * mm});
            skCircle(sketch, "E9.0.1.58", {"center": v(-104.33, -61.28) * mm, "radius": 2.38 * mm});
            skCircle(sketch, "E9.0.1.59", {"center": v(14.29, -51.75) * mm, "radius": 2.38 * mm});
            skCircle(sketch, "E9.0.1.60", {"center": v(94.8, -61.28) * mm, "radius": 2.38 * mm});
            skCircle(sketch, "E9.0.1.61", {"center": v(24.2, -32.7) * mm, "radius": 2.38 * mm});
            skCircle(sketch, "E9.0.1.62", {"center": v(-33.72, -61.28) * mm, "radius": 2.38 * mm});
            skCircle(sketch, "E9.0.1.63", {"center": v(-81.72, -42.23) * mm, "radius": 2.38 * mm});
            skCircle(sketch, "E9.0.1.64", {"center": v(-33.72, -32.7) * mm, "radius": 2.38 * mm});
            skCircle(sketch, "E9.0.1.65", {"center": v(14.29, -61.28) * mm, "radius": 2.38 * mm});
            skCircle(sketch, "E9.0.1.66", {"center": v(-69.02, -32.7) * mm, "radius": 2.38 * mm});
            skCircle(sketch, "E9.0.1.67", {"center": v(-81.72, -32.7) * mm, "radius": 2.38 * mm});
            skCircle(sketch, "E9.0.1.68", {"center": v(-33.72, -51.75) * mm, "radius": 2.38 * mm});
            skLineSegment(sketch, "E9.0.1.69", {"start": v(-11.11, -61.28) * mm, "end": v(24.2, -61.28) * mm, "construction": true});
            skCircle(sketch, "E9.0.1.70", {"center": v(-27.37, -32.7) * mm, "radius": 2.38 * mm});
            skCircle(sketch, "E9.0.1.71", {"center": v(36.9, -51.75) * mm, "radius": 2.38 * mm});
            skCircle(sketch, "E9.0.1.72", {"center": v(-75.37, -51.75) * mm, "radius": 2.38 * mm});
            skCircle(sketch, "E9.0.1.73", {"center": v(24.2, -42.23) * mm, "radius": 2.38 * mm});
            skCircle(sketch, "E9.0.1.74", {"center": v(107.5, -61.28) * mm, "radius": 2.38 * mm});
            skCircle(sketch, "E9.0.1.75", {"center": v(-21.02, -42.23) * mm, "radius": 2.38 * mm});
            skCircle(sketch, "E9.0.1.76", {"center": v(59.5, -32.7) * mm, "radius": 2.38 * mm});
            skCircle(sketch, "E9.0.1.77", {"center": v(84.9, -61.28) * mm, "radius": 2.38 * mm});
            skCircle(sketch, "E9.0.1.78", {"center": v(43.24, -32.7) * mm, "radius": 2.38 * mm});
            skCircle(sketch, "E9.0.1.79", {"center": v(-62.67, -32.7) * mm, "radius": 2.38 * mm});
            skCircle(sketch, "E9.0.1.80", {"center": v(72.2, -51.75) * mm, "radius": 2.38 * mm});
            skCircle(sketch, "E9.0.1.81", {"center": v(-110.68, -51.75) * mm, "radius": 2.38 * mm});
            skCircle(sketch, "E9.0.1.82", {"center": v(-11.11, -32.7) * mm, "radius": 2.38 * mm});
            skCircle(sketch, "E9.0.1.83", {"center": v(1.59, -32.7) * mm, "radius": 2.38 * mm});
            skCircle(sketch, "E9.0.1.84", {"center": v(-110.68, -42.23) * mm, "radius": 2.38 * mm});
            skCircle(sketch, "E9.0.1.85", {"center": v(-4.76, -42.23) * mm, "radius": 2.38 * mm});
            skCircle(sketch, "E9.0.1.86", {"center": v(-117.03, -51.75) * mm, "radius": 2.38 * mm});
            skCircle(sketch, "E9.0.1.87", {"center": v(-40.07, -61.28) * mm, "radius": 2.38 * mm});
            skCircle(sketch, "E9.0.1.88", {"center": v(1.59, -61.28) * mm, "radius": 2.38 * mm});
            skCircle(sketch, "E9.0.1.89", {"center": v(-27.37, -61.28) * mm, "radius": 2.38 * mm});
            skCircle(sketch, "E9.0.1.90", {"center": v(65.85, -51.75) * mm, "radius": 2.38 * mm});
            skCircle(sketch, "E9.0.1.91", {"center": v(-117.03, -32.7) * mm, "radius": 2.38 * mm});
            skCircle(sketch, "E9.0.1.92", {"center": v(-97.98, -32.7) * mm, "radius": 2.38 * mm});
            skCircle(sketch, "E9.0.1.93", {"center": v(101.16, -32.7) * mm, "radius": 2.38 * mm});
            skCircle(sketch, "E9.0.1.94", {"center": v(-46.42, -61.28) * mm, "radius": 2.38 * mm});
            skCircle(sketch, "E9.0.1.95", {"center": v(120.2, -32.7) * mm, "radius": 2.38 * mm});
            skCircle(sketch, "E9.0.1.96", {"center": v(84.9, -51.75) * mm, "radius": 2.38 * mm});
            skCircle(sketch, "E9.0.1.97", {"center": v(72.2, -61.28) * mm, "radius": 2.38 * mm});
            skCircle(sketch, "E9.0.1.98", {"center": v(107.5, -32.7) * mm, "radius": 2.38 * mm});
            skCircle(sketch, "E9.0.1.99", {"center": v(65.85, -32.7) * mm, "radius": 2.38 * mm});
            skCircle(sketch, "E9.0.1.100", {"center": v(24.2, -51.75) * mm, "radius": 2.38 * mm});
            skCircle(sketch, "E9.0.1.101", {"center": v(113.86, -32.7) * mm, "radius": 2.38 * mm});
            skCircle(sketch, "E9.0.1.102", {"center": v(-4.76, -51.75) * mm, "radius": 2.38 * mm});
            skCircle(sketch, "E9.0.1.103", {"center": v(101.16, -42.23) * mm, "radius": 2.38 * mm});
            skCircle(sketch, "E9.0.1.104", {"center": v(84.9, -42.23) * mm, "radius": 2.38 * mm});
            skCircle(sketch, "E9.0.1.105", {"center": v(72.2, -32.7) * mm, "radius": 2.38 * mm});
            skCircle(sketch, "E9.0.1.106", {"center": v(113.86, -61.28) * mm, "radius": 2.38 * mm});
            skCircle(sketch, "E9.0.1.107", {"center": v(24.2, -61.28) * mm, "radius": 2.38 * mm});
            skCircle(sketch, "E9.0.1.108", {"center": v(49.6, -61.28) * mm, "radius": 2.38 * mm});
            skCircle(sketch, "E9.0.1.109", {"center": v(84.9, -32.7) * mm, "radius": 2.38 * mm});
            skCircle(sketch, "E9.0.1.110", {"center": v(59.5, -61.28) * mm, "radius": 2.38 * mm});
            skCircle(sketch, "E9.0.1.111", {"center": v(36.9, -32.7) * mm, "radius": 2.38 * mm});
            skCircle(sketch, "E9.0.1.112", {"center": v(36.9, -61.28) * mm, "radius": 2.38 * mm});
            skCircle(sketch, "E9.0.1.113", {"center": v(78.55, -61.28) * mm, "radius": 2.38 * mm});
            skCircle(sketch, "E9.0.1.114", {"center": v(101.16, -51.75) * mm, "radius": 2.38 * mm});
            skCircle(sketch, "E9.0.1.115", {"center": v(-75.37, -32.7) * mm, "radius": 2.38 * mm});
            skCircle(sketch, "E9.0.1.116", {"center": v(-46.42, -32.7) * mm, "radius": 2.38 * mm});
            skCircle(sketch, "E9.0.1.117", {"center": v(-81.72, -61.28) * mm, "radius": 2.38 * mm});
            skCircle(sketch, "E9.0.1.118", {"center": v(-4.76, -61.28) * mm, "radius": 2.38 * mm});
            skCircle(sketch, "E9.0.1.119", {"center": v(-56.32, -61.28) * mm, "radius": 2.38 * mm});
            skCircle(sketch, "E9.0.1.120", {"center": v(-40.07, -32.7) * mm, "radius": 2.38 * mm});
            skCircle(sketch, "E9.0.1.121", {"center": v(-46.42, -42.23) * mm, "radius": 2.38 * mm});
            skCircle(sketch, "E9.0.1.122", {"center": v(78.55, -42.23) * mm, "radius": 2.38 * mm});
            skCircle(sketch, "E9.0.1.123", {"center": v(-11.11, -42.23) * mm, "radius": 2.38 * mm});
            skCircle(sketch, "E9.0.1.124", {"center": v(-117.03, -42.23) * mm, "radius": 2.38 * mm});
            skCircle(sketch, "E9.0.1.125", {"center": v(30.54, -42.23) * mm, "radius": 2.38 * mm});
            skCircle(sketch, "E9.0.1.126", {"center": v(-62.67, -42.23) * mm, "radius": 2.38 * mm});
            skCircle(sketch, "E9.0.1.127", {"center": v(14.29, -42.23) * mm, "radius": 2.38 * mm});
            skCircle(sketch, "E9.0.1.128", {"center": v(-75.37, -42.23) * mm, "radius": 2.38 * mm});
            skCircle(sketch, "E9.0.1.129", {"center": v(-56.32, -42.23) * mm, "radius": 2.38 * mm});
            skCircle(sketch, "E9.0.1.130", {"center": v(-97.98, -42.23) * mm, "radius": 2.38 * mm});
            skCircle(sketch, "E9.0.1.131", {"center": v(-104.33, -42.23) * mm, "radius": 2.38 * mm});
            skCircle(sketch, "E9.0.1.132", {"center": v(59.5, -42.23) * mm, "radius": 2.38 * mm});
            skCircle(sketch, "E9.0.1.133", {"center": v(-33.72, -42.23) * mm, "radius": 2.38 * mm});
            skCircle(sketch, "E9.0.1.134", {"center": v(1.59, -42.23) * mm, "radius": 2.38 * mm});
            skCircle(sketch, "E9.0.1.135", {"center": v(65.85, -42.23) * mm, "radius": 2.38 * mm});
            skCircle(sketch, "E9.0.1.136", {"center": v(113.86, -42.23) * mm, "radius": 2.38 * mm});
            skCircle(sketch, "E9.0.1.137", {"center": v(107.5, -42.23) * mm, "radius": 2.38 * mm});
            skCircle(sketch, "E9.0.1.138", {"center": v(94.8, -42.23) * mm, "radius": 2.38 * mm});
            skCircle(sketch, "E9.0.1.139", {"center": v(43.24, -42.23) * mm, "radius": 2.38 * mm});
            skCircle(sketch, "E9.0.1.140", {"center": v(-27.37, -42.23) * mm, "radius": 2.38 * mm});
            skCircle(sketch, "E9.0.1.141", {"center": v(49.6, -42.23) * mm, "radius": 2.38 * mm});
            skCircle(sketch, "E10.1.0.0", {"center": v(-145.99, 61.28) * mm, "radius": 2.38 * mm});
            skCircle(sketch, "E10.1.0.1", {"center": v(-126.94, 32.7) * mm, "radius": 2.38 * mm});
            skCircle(sketch, "E10.1.0.2", {"center": v(-126.94, 61.28) * mm, "radius": 2.38 * mm});
            skCircle(sketch, "E10.1.0.3", {"center": v(-133.29, 32.7) * mm, "radius": 2.38 * mm});
            skCircle(sketch, "E10.1.0.4", {"center": v(-139.64, 61.28) * mm, "radius": 2.38 * mm});
            skCircle(sketch, "E10.1.0.5", {"center": v(-133.29, 61.28) * mm, "radius": 2.38 * mm});
            skCircle(sketch, "E10.1.0.6", {"center": v(-152.34, 51.75) * mm, "radius": 2.38 * mm});
            skCircle(sketch, "E10.1.0.7", {"center": v(-133.29, 42.23) * mm, "radius": 2.38 * mm});
            skCircle(sketch, "E10.1.0.8", {"center": v(-145.99, 32.7) * mm, "radius": 2.38 * mm});
            skCircle(sketch, "E10.1.0.9", {"center": v(-133.29, 51.75) * mm, "radius": 2.38 * mm});
            skCircle(sketch, "E10.1.0.10", {"center": v(-152.34, 32.7) * mm, "radius": 2.38 * mm});
            skCircle(sketch, "E10.1.0.11", {"center": v(-126.94, 51.75) * mm, "radius": 2.38 * mm});
            skCircle(sketch, "E10.1.0.12", {"center": v(-139.64, 42.23) * mm, "radius": 2.38 * mm});
            skCircle(sketch, "E10.1.0.13", {"center": v(-139.64, 32.7) * mm, "radius": 2.38 * mm});
            skCircle(sketch, "E10.1.0.14", {"center": v(-126.94, 42.23) * mm, "radius": 2.38 * mm});
            skCircle(sketch, "E10.1.0.15", {"center": v(-145.99, 51.75) * mm, "radius": 2.38 * mm});
            skCircle(sketch, "E10.1.0.16", {"center": v(-139.64, 51.75) * mm, "radius": 2.38 * mm});
            skCircle(sketch, "E10.1.0.17", {"center": v(-152.34, 42.23) * mm, "radius": 2.38 * mm});
            skCircle(sketch, "E10.1.0.18", {"center": v(-152.34, 61.28) * mm, "radius": 2.38 * mm});
            skCircle(sketch, "E10.1.0.19", {"center": v(-145.99, 42.23) * mm, "radius": 2.38 * mm});
            skCircle(sketch, "E11.1.0.0", {"center": v(158.3, -51.75) * mm, "radius": 2.38 * mm});
            skCircle(sketch, "E11.1.0.1", {"center": v(158.3, -42.23) * mm, "radius": 2.38 * mm});
            skCircle(sketch, "E11.1.0.2", {"center": v(145.6, -61.28) * mm, "radius": 2.38 * mm});
            skCircle(sketch, "E11.1.0.3", {"center": v(158.3, -32.7) * mm, "radius": 2.38 * mm});
            skCircle(sketch, "E11.1.0.4", {"center": v(145.6, -42.23) * mm, "radius": 2.38 * mm});
            skCircle(sketch, "E11.1.0.5", {"center": v(145.6, -32.7) * mm, "radius": 2.38 * mm});
            skCircle(sketch, "E11.1.0.6", {"center": v(145.6, -51.75) * mm, "radius": 2.38 * mm});
            skCircle(sketch, "E11.1.0.7", {"center": v(151.96, -51.75) * mm, "radius": 2.38 * mm});
            skCircle(sketch, "E11.1.0.8", {"center": v(151.96, -32.7) * mm, "radius": 2.38 * mm});
            skCircle(sketch, "E11.1.0.9", {"center": v(151.96, -42.23) * mm, "radius": 2.38 * mm});
            skCircle(sketch, "E11.1.0.10", {"center": v(158.3, -61.28) * mm, "radius": 2.38 * mm});
            skCircle(sketch, "E11.1.0.11", {"center": v(151.96, -61.28) * mm, "radius": 2.38 * mm});
            skCircle(sketch, "E12.1.0.0", {"center": v(-130.11, -51.75) * mm, "radius": 2.38 * mm});
            skCircle(sketch, "E12.1.0.1", {"center": v(-130.11, -42.23) * mm, "radius": 2.38 * mm});
            skCircle(sketch, "E12.1.0.2", {"center": v(-130.11, -61.28) * mm, "radius": 2.38 * mm});
            skCircle(sketch, "E12.1.0.3", {"center": v(-130.11, -32.7) * mm, "radius": 2.38 * mm});
            skCircle(sketch, "E13.1.0", {"center": v(-150.1, -43.48) * mm, "radius": 2.38 * mm});
            skCircle(sketch, "E13.1.1", {"center": v(-143.36, -36.74) * mm, "radius": 2.38 * mm});
            skCircle(sketch, "E13.1.2", {"center": v(-156.83, -50.21) * mm, "radius": 2.38 * mm});
            skCircle(sketch, "E13.1.3", {"center": v(-136.62, -30) * mm, "radius": 2.38 * mm});
            skCircle(sketch, "E13.2.0", {"center": v(-158.37, -23.5) * mm, "radius": 2.38 * mm});
            skCircle(sketch, "E13.2.1", {"center": v(-148.84, -23.5) * mm, "radius": 2.38 * mm});
            skCircle(sketch, "E13.2.2", {"center": v(-167.9, -23.5) * mm, "radius": 2.38 * mm});
            skCircle(sketch, "E13.2.3", {"center": v(-139.32, -23.5) * mm, "radius": 2.38 * mm});
            skCircle(sketch, "E13.3.0", {"center": v(-150.1, -3.51) * mm, "radius": 2.38 * mm});
            skCircle(sketch, "E13.3.1", {"center": v(-143.36, -10.25) * mm, "radius": 2.38 * mm});
            skCircle(sketch, "E13.3.2", {"center": v(-156.83, 3.22) * mm, "radius": 2.38 * mm});
            skCircle(sketch, "E13.3.3", {"center": v(-136.62, -16.98) * mm, "radius": 2.38 * mm});
            skCircle(sketch, "E13.4.0", {"center": v(-130.11, 4.76) * mm, "radius": 2.38 * mm});
            skCircle(sketch, "E13.4.1", {"center": v(-130.11, -4.76) * mm, "radius": 2.38 * mm});
            skCircle(sketch, "E13.4.2", {"center": v(-130.11, 14.29) * mm, "radius": 2.38 * mm});
            skCircle(sketch, "E13.4.3", {"center": v(-130.11, -14.29) * mm, "radius": 2.38 * mm});
            skPoint(sketch, "E13.center", {"position": v(-130.11, -23.5) * mm});
            skCircle(sketch, "E14.1.0.0", {"center": v(130.11, 32.7) * mm, "radius": 2.38 * mm});
            skCircle(sketch, "E14.1.0.1", {"center": v(130.11, 42.23) * mm, "radius": 2.38 * mm});
            skCircle(sketch, "E14.1.0.2", {"center": v(130.11, 51.75) * mm, "radius": 2.38 * mm});
            skCircle(sketch, "E14.1.0.3", {"center": v(130.11, 61.28) * mm, "radius": 2.38 * mm});
            skCircle(sketch, "E15.1.0", {"center": v(150.1, 43.48) * mm, "radius": 2.38 * mm});
            skCircle(sketch, "E15.1.1", {"center": v(143.36, 36.74) * mm, "radius": 2.38 * mm});
            skCircle(sketch, "E15.1.2", {"center": v(156.83, 50.21) * mm, "radius": 2.38 * mm});
            skCircle(sketch, "E15.1.3", {"center": v(136.62, 30) * mm, "radius": 2.38 * mm});
            skCircle(sketch, "E15.2.0", {"center": v(158.37, 23.5) * mm, "radius": 2.38 * mm});
            skCircle(sketch, "E15.2.1", {"center": v(148.84, 23.5) * mm, "radius": 2.38 * mm});
            skCircle(sketch, "E15.2.2", {"center": v(167.9, 23.5) * mm, "radius": 2.38 * mm});
            skCircle(sketch, "E15.2.3", {"center": v(139.32, 23.5) * mm, "radius": 2.38 * mm});
            skCircle(sketch, "E15.3.0", {"center": v(150.1, 3.51) * mm, "radius": 2.38 * mm});
            skCircle(sketch, "E15.3.1", {"center": v(143.36, 10.25) * mm, "radius": 2.38 * mm});
            skCircle(sketch, "E15.3.2", {"center": v(156.83, -3.22) * mm, "radius": 2.38 * mm});
            skCircle(sketch, "E15.3.3", {"center": v(136.62, 16.98) * mm, "radius": 2.38 * mm});
            skCircle(sketch, "E15.4.0", {"center": v(130.11, -4.76) * mm, "radius": 2.38 * mm});
            skCircle(sketch, "E15.4.1", {"center": v(130.11, 4.76) * mm, "radius": 2.38 * mm});
            skCircle(sketch, "E15.4.2", {"center": v(130.11, -14.29) * mm, "radius": 2.38 * mm});
            skCircle(sketch, "E15.4.3", {"center": v(130.11, 14.29) * mm, "radius": 2.38 * mm});
            skPoint(sketch, "E15.center", {"position": v(130.11, 23.5) * mm});
            skSolve(sketch);
        }
        {
            var Q0;
            Q0=qSketchRegion(id+"F2",true);
            extrude(context, id + "F3", {"entities" : qUnion([Q0]), "operationType" : NewBodyOperationType.REMOVE, "oppositeDirection" : true, "depth" : 9.52 * mm, "offsetDistance" : 25 * mm});
        }
        {
            var Q0;
            Q0=makeQuery(id+"F1.opExtrude","CAP_FACE",FACE,{"disambiguationData":[OSD([sQuery(id+"F0.wireOp",EDGE,"E0.bottom"),sQuery(id+"F0.wireOp",EDGE,"E0.top"),sQuery(id+"F0.wireOp",EDGE,"E0.left"),sQuery(id+"F0.wireOp",EDGE,"E0.right")])],"isStart":false});
            var sketch = newSketch(context, id + "F4", { "sketchPlane" : qUnion([Q0])});
            skPoint(sketch, "E16.middle", {"position": v(75.34, 0) * mm});
            skPoint(sketch, "E17.middle", {"position": v(-86, 0) * mm});
            skCircle(sketch, "E18", {"center": v(-171.45, 57.15) * mm, "radius": 4 * mm});
            skCircle(sketch, "E19", {"center": v(171.45, 57.15) * mm, "radius": 4 * mm});
            skSolve(sketch);
        }
        {
            var Q0;
            Q0=makeQuery(id+"F4.imprint","IMPRINT",FACE,{"disambiguationData":[TD([[makeQuery(id+"F4.imprint","IMPRINT",EDGE,{"derivedFrom":sQuery(id+"F4.wireOp",EDGE,"E18")}),1.0]])]});
            var Q1;
            Q1=makeQuery(id+"F4.imprint","IMPRINT",FACE,{"disambiguationData":[TD([[makeQuery(id+"F4.imprint","IMPRINT",EDGE,{"derivedFrom":sQuery(id+"F4.wireOp",EDGE,"E19")}),1.0]])]});
            extrude(context, id + "F5", {"entities" : qUnion([Q0, Q1]), "operationType" : NewBodyOperationType.REMOVE, "oppositeDirection" : true, "depth" : 5 * mm, "offsetDistance" : 25 * mm});
        }
        {
            var Q0;
            Q0=makeQuery(id+"F1.opExtrude","CAP_FACE",FACE,{"disambiguationData":[OSD([sQuery(id+"F0.wireOp",EDGE,"E0.bottom"),sQuery(id+"F0.wireOp",EDGE,"E0.top"),sQuery(id+"F0.wireOp",EDGE,"E0.left"),sQuery(id+"F0.wireOp",EDGE,"E0.right")])],"isStart":true});
            var sketch = newSketch(context, id + "F6", { "sketchPlane" : qUnion([Q0])});
            skLineSegment(sketch, "E20.bottom", {"start": v(140.53, -27.62) * mm, "end": v(163.39, -27.62) * mm});
            skLineSegment(sketch, "E20.top", {"start": v(140.53, -66.36) * mm, "end": v(163.39, -66.36) * mm});
            skLineSegment(sketch, "E20.right", {"start": v(163.39, -27.62) * mm, "end": v(163.39, -66.36) * mm});
            skPoint(sketch, "E21.middle", {"position": v(-166.62, 47) * mm});
            skArc(sketch, "E22", {"start": v(129.73, 66.36) * mm, "mid": v(172.6, 23.5) * mm, "end": v(129.73, -19.37) * mm});
            skArc(sketch, "E23", {"start": v(129.73, 27.62) * mm, "mid": v(133.86, 23.5) * mm, "end": v(129.73, 19.37) * mm});
            skArc(sketch, "E24", {"start": v(-129.73, 19.37) * mm, "mid": v(-172.6, -23.5) * mm, "end": v(-129.73, -66.36) * mm});
            skArc(sketch, "E25", {"start": v(-129.73, -19.37) * mm, "mid": v(-133.86, -23.5) * mm, "end": v(-129.73, -27.62) * mm});
            skLineSegment(sketch, "E26", {"start": v(126.56, -27.62) * mm, "end": v(126.56, -66.36) * mm});
            skLineSegment(sketch, "E27", {"start": v(140.53, -27.62) * mm, "end": v(140.53, -66.36) * mm});
            skLineSegment(sketch, "E28", {"start": v(-158.69, 66.36) * mm, "end": v(-158.69, 54.93) * mm});
            skLineSegment(sketch, "E29", {"start": v(-158.69, 39.05) * mm, "end": v(-158.69, 27.62) * mm});
            skLineSegment(sketch, "E30", {"start": v(-158.69, 66.36) * mm, "end": v(129.73, 66.36) * mm});
            skLineSegment(sketch, "E31", {"start": v(129.73, 27.62) * mm, "end": v(-158.69, 27.62) * mm});
            skLineSegment(sketch, "E32", {"start": v(-129.73, 19.37) * mm, "end": v(129.73, 19.37) * mm});
            skLineSegment(sketch, "E33", {"start": v(129.73, -19.37) * mm, "end": v(-129.73, -19.37) * mm});
            skLineSegment(sketch, "E34", {"start": v(-129.73, -27.62) * mm, "end": v(126.56, -27.62) * mm});
            skLineSegment(sketch, "E35", {"start": v(126.56, -66.36) * mm, "end": v(-129.73, -66.36) * mm});
            skLineSegment(sketch, "E36.bottom", {"start": v(-158.69, 39.05) * mm, "end": v(-174.56, 39.05) * mm});
            skLineSegment(sketch, "E36.top", {"start": v(-158.69, 54.93) * mm, "end": v(-174.56, 54.93) * mm});
            skLineSegment(sketch, "E36.right", {"start": v(-174.56, 39.05) * mm, "end": v(-174.56, 54.93) * mm});
            skSolve(sketch);
        }
        {
            var Q0;
            Q0=qSketchRegion(id+"F6",true);
            extrude(context, id + "F7", {"entities" : qUnion([Q0]), "operationType" : NewBodyOperationType.REMOVE, "oppositeDirection" : true, "depth" : 3.17 * mm, "offsetDistance" : 25.4 * mm});
        }
        {
            var Q0;
            Q0=makeQuery(id+"F6.imprint","IMPRINT",FACE,{"disambiguationData":[TD([[makeQuery(id+"F6.imprint","IMPRINT",EDGE,{"derivedFrom":sQuery(id+"F6.wireOp",EDGE,"E22")}),-1.0]])]});
            var Q1;
            Q1=makeQuery(id+"F6.imprint","IMPRINT",FACE,{"disambiguationData":[TD([[makeQuery(id+"F6.imprint","IMPRINT",EDGE,{"derivedFrom":sQuery(id+"F6.wireOp",EDGE,"E20.bottom")}),-1.0]])]});
            extrude(context, id + "F8", {"entities" : qUnion([Q0, Q1]), "oppositeDirection" : true, "depth" : 3.17 * mm, "offsetDistance" : 25.4 * mm});
        }
        {
            var Q0;
            Q0=makeQuery(id+"F8.opExtrude","SWEPT_EDGE",EDGE,{"disambiguationData":[OSD([sQuery(id+"F6.wireOp",EDGE,"E21.top"),sQuery(id+"F6.wireOp",EDGE,"E21.right")])]});
            var Q1;
            Q1=makeQuery(id+"F8.opExtrude","SWEPT_EDGE",EDGE,{"disambiguationData":[OSD([sQuery(id+"F6.wireOp",EDGE,"E21.bottom"),sQuery(id+"F6.wireOp",EDGE,"E21.right")])]});
            var Q2;
            Q2=makeQuery(id+"F8.opExtrude","SWEPT_EDGE",EDGE,{"disambiguationData":[OSD([sQuery(id+"F6.wireOp",EDGE,"E21.bottom"),sQuery(id+"F6.wireOp",EDGE,"E29")])]});
            var Q3;
            Q3=makeQuery(id+"F8.opExtrude","SWEPT_EDGE",EDGE,{"disambiguationData":[OSD([sQuery(id+"F6.wireOp",EDGE,"E29"),sQuery(id+"F6.wireOp",EDGE,"E31")])]});
            var Q4;
            Q4=makeQuery(id+"F8.opExtrude","SWEPT_EDGE",EDGE,{"disambiguationData":[OSD([sQuery(id+"F6.wireOp",EDGE,"E28"),sQuery(id+"F6.wireOp",EDGE,"E30")])]});
            var Q5;
            Q5=makeQuery(id+"F8.opExtrude","SWEPT_EDGE",EDGE,{"disambiguationData":[OSD([sQuery(id+"F6.wireOp",EDGE,"E21.top"),sQuery(id+"F6.wireOp",EDGE,"E28")])]});
            var Q6;
            Q6=makeQuery(id+"F8.opExtrude","SWEPT_EDGE",EDGE,{"disambiguationData":[OSD([sQuery(id+"F6.wireOp",EDGE,"E26"),sQuery(id+"F6.wireOp",EDGE,"E34")])]});
            var Q7;
            Q7=makeQuery(id+"F8.opExtrude","SWEPT_EDGE",EDGE,{"disambiguationData":[OSD([sQuery(id+"F6.wireOp",EDGE,"E20.bottom"),sQuery(id+"F6.wireOp",EDGE,"E27")])]});
            var Q8;
            Q8=makeQuery(id+"F8.opExtrude","SWEPT_EDGE",EDGE,{"disambiguationData":[OSD([sQuery(id+"F6.wireOp",EDGE,"E20.bottom"),sQuery(id+"F6.wireOp",EDGE,"E20.right")])]});
            var Q9;
            Q9=makeQuery(id+"F8.opExtrude","SWEPT_EDGE",EDGE,{"disambiguationData":[OSD([sQuery(id+"F6.wireOp",EDGE,"E20.top"),sQuery(id+"F6.wireOp",EDGE,"E27")])]});
            var Q10;
            Q10=makeQuery(id+"F8.opExtrude","SWEPT_EDGE",EDGE,{"disambiguationData":[OSD([sQuery(id+"F6.wireOp",EDGE,"E20.top"),sQuery(id+"F6.wireOp",EDGE,"E20.right")])]});
            var Q11;
            Q11=makeQuery(id+"F8.opExtrude","SWEPT_EDGE",EDGE,{"disambiguationData":[OSD([sQuery(id+"F6.wireOp",EDGE,"E26"),sQuery(id+"F6.wireOp",EDGE,"E35")])]});
            var Q12;
            Q12=makeQuery(id+"F8.opExtrude","SWEPT_EDGE",EDGE,{"disambiguationData":[OSD([sQuery(id+"F6.wireOp",EDGE,"E36.top"),sQuery(id+"F6.wireOp",EDGE,"E36.right")])]});
            var Q13;
            Q13=makeQuery(id+"F8.opExtrude","SWEPT_EDGE",EDGE,{"disambiguationData":[OSD([sQuery(id+"F6.wireOp",EDGE,"E36.bottom"),sQuery(id+"F6.wireOp",EDGE,"E36.right")])]});
            fillet(context, id + "F9", {"entities" : qUnion([Q0, Q1, Q2, Q3, Q4, Q5, Q6, Q7, Q8, Q9, Q10, Q11, Q12, Q13]), "radius" : 3.17 * mm, "tangentPropagation" : true, "allowEdgeOverflow" : false});
        }
        {
            var Q0;
            Q0=makeQuery(id+"F7.boolean.opBoolean","COPY",EDGE,{"derivedFrom":makeQuery(id+"F7.opExtrude","SWEPT_EDGE",EDGE,{"disambiguationData":[OSD([sQuery(id+"F6.wireOp",EDGE,"E36.top"),sQuery(id+"F6.wireOp",EDGE,"E36.right")])]})});
            var Q1;
            Q1=makeQuery(id+"F7.boolean.opBoolean","COPY",EDGE,{"derivedFrom":makeQuery(id+"F7.opExtrude","SWEPT_EDGE",EDGE,{"disambiguationData":[OSD([sQuery(id+"F6.wireOp",EDGE,"E29"),sQuery(id+"F6.wireOp",EDGE,"E36.bottom")])]})});
            var Q2;
            Q2=makeQuery(id+"F7.boolean.opBoolean","COPY",EDGE,{"derivedFrom":makeQuery(id+"F7.opExtrude","SWEPT_EDGE",EDGE,{"disambiguationData":[OSD([sQuery(id+"F6.wireOp",EDGE,"E28"),sQuery(id+"F6.wireOp",EDGE,"E36.top")])]})});
            var Q3;
            Q3=makeQuery(id+"F7.boolean.opBoolean","COPY",EDGE,{"derivedFrom":makeQuery(id+"F7.opExtrude","SWEPT_EDGE",EDGE,{"disambiguationData":[OSD([sQuery(id+"F6.wireOp",EDGE,"E28"),sQuery(id+"F6.wireOp",EDGE,"E30")])]})});
            var Q4;
            Q4=makeQuery(id+"F7.boolean.opBoolean","COPY",EDGE,{"derivedFrom":makeQuery(id+"F7.opExtrude","SWEPT_EDGE",EDGE,{"disambiguationData":[OSD([sQuery(id+"F6.wireOp",EDGE,"E36.bottom"),sQuery(id+"F6.wireOp",EDGE,"E36.right")])]})});
            var Q5;
            Q5=makeQuery(id+"F7.boolean.opBoolean","COPY",EDGE,{"derivedFrom":makeQuery(id+"F7.opExtrude","SWEPT_EDGE",EDGE,{"disambiguationData":[OSD([sQuery(id+"F6.wireOp",EDGE,"E29"),sQuery(id+"F6.wireOp",EDGE,"E31")])]})});
            var Q6;
            Q6=makeQuery(id+"F7.boolean.opBoolean","COPY",EDGE,{"derivedFrom":makeQuery(id+"F7.opExtrude","SWEPT_EDGE",EDGE,{"disambiguationData":[OSD([sQuery(id+"F6.wireOp",EDGE,"E20.bottom"),sQuery(id+"F6.wireOp",EDGE,"E27")])]})});
            var Q7;
            Q7=makeQuery(id+"F7.boolean.opBoolean","COPY",EDGE,{"derivedFrom":makeQuery(id+"F7.opExtrude","SWEPT_EDGE",EDGE,{"disambiguationData":[OSD([sQuery(id+"F6.wireOp",EDGE,"E26"),sQuery(id+"F6.wireOp",EDGE,"E35")])]})});
            var Q8;
            Q8=makeQuery(id+"F7.boolean.opBoolean","COPY",EDGE,{"derivedFrom":makeQuery(id+"F7.opExtrude","SWEPT_EDGE",EDGE,{"disambiguationData":[OSD([sQuery(id+"F6.wireOp",EDGE,"E20.top"),sQuery(id+"F6.wireOp",EDGE,"E20.right")])]})});
            var Q9;
            Q9=makeQuery(id+"F7.boolean.opBoolean","COPY",EDGE,{"derivedFrom":makeQuery(id+"F7.opExtrude","SWEPT_EDGE",EDGE,{"disambiguationData":[OSD([sQuery(id+"F6.wireOp",EDGE,"E26"),sQuery(id+"F6.wireOp",EDGE,"E34")])]})});
            var Q10;
            Q10=makeQuery(id+"F7.boolean.opBoolean","COPY",EDGE,{"derivedFrom":makeQuery(id+"F7.opExtrude","SWEPT_EDGE",EDGE,{"disambiguationData":[OSD([sQuery(id+"F6.wireOp",EDGE,"E20.bottom"),sQuery(id+"F6.wireOp",EDGE,"E20.right")])]})});
            var Q11;
            Q11=makeQuery(id+"F7.boolean.opBoolean","COPY",EDGE,{"derivedFrom":makeQuery(id+"F7.opExtrude","SWEPT_EDGE",EDGE,{"disambiguationData":[OSD([sQuery(id+"F6.wireOp",EDGE,"E20.top"),sQuery(id+"F6.wireOp",EDGE,"E27")])]})});
            fillet(context, id + "F10", {"entities" : qUnion([Q0, Q1, Q2, Q3, Q4, Q5, Q6, Q7, Q8, Q9, Q10, Q11]), "radius" : 3.17 * mm, "tangentPropagation" : true, "allowEdgeOverflow" : false});
        }
        {
            var Q0;
            Q0=makeQuery(id+"F1.opExtrude","CAP_FACE",FACE,{"disambiguationData":[OSD([sQuery(id+"F0.wireOp",EDGE,"E0.bottom"),sQuery(id+"F0.wireOp",EDGE,"E0.top"),sQuery(id+"F0.wireOp",EDGE,"E0.left"),sQuery(id+"F0.wireOp",EDGE,"E0.right")])],"isStart":false});
            var sketch = newSketch(context, id + "F11", { "sketchPlane" : qUnion([Q0])});
            skCircle(sketch, "E37", {"center": v(-171.45, -69.5) * mm, "radius": 5 * mm});
            skCircle(sketch, "E38", {"center": v(171.45, -69.5) * mm, "radius": 5 * mm});
            skSolve(sketch);
        }
        {
            var Q0;
            Q0=makeQuery(id+"F11.imprint","IMPRINT",FACE,{"disambiguationData":[TD([[makeQuery(id+"F11.imprint","IMPRINT",EDGE,{"derivedFrom":sQuery(id+"F11.wireOp",EDGE,"E38")}),1.0]])]});
            var Q1;
            Q1=makeQuery(id+"F11.imprint","IMPRINT",FACE,{"disambiguationData":[TD([[makeQuery(id+"F11.imprint","IMPRINT",EDGE,{"derivedFrom":sQuery(id+"F11.wireOp",EDGE,"E37")}),1.0]])]});
            extrude(context, id + "F12", {"entities" : qUnion([Q0, Q1]), "operationType" : NewBodyOperationType.REMOVE, "oppositeDirection" : true, "depth" : 11.5 * mm, "offsetDistance" : 25 * mm});
        }
        {
            var Q0;
            Q0=makeQuery(id+"F1.opExtrude","CAP_FACE",FACE,{"disambiguationData":[OSD([sQuery(id+"F0.wireOp",EDGE,"E0.bottom"),sQuery(id+"F0.wireOp",EDGE,"E0.top"),sQuery(id+"F0.wireOp",EDGE,"E0.left"),sQuery(id+"F0.wireOp",EDGE,"E0.right")])],"isStart":false});
            var sketch = newSketch(context, id + "F13", { "sketchPlane" : qUnion([Q0])});
            skLineSegment(sketch, "E39", {"start": v(190.5, 16.7) * mm, "end": v(142.88, 16.7) * mm});
            skLineSegment(sketch, "E40", {"start": v(125.58, 76.2) * mm, "end": v(125.58, 34.93) * mm});
            skLineSegment(sketch, "E41.bottom", {"start": v(142.88, 34.93) * mm, "end": v(47.63, 34.93) * mm});
            skLineSegment(sketch, "E41.top", {"start": v(142.88, -34.92) * mm, "end": v(47.63, -34.92) * mm});
            skLineSegment(sketch, "E41.left", {"start": v(142.88, 34.93) * mm, "end": v(142.88, -34.92) * mm});
            skLineSegment(sketch, "E41.right", {"start": v(47.63, 34.93) * mm, "end": v(47.63, -34.92) * mm});
            skSolve(sketch);
        }
        {
            var Q0;
            {var subQ4=sQuery(id+"F13.wireOp",EDGE,"E41.top");Q0=makeQuery(id+"F13.imprint","IMPRINT",FACE,{"disambiguationData":[TD([[makeQuery(id+"F13.imprint","IMPRINT",EDGE,{"derivedFrom":subQ4}),-1.0]])]});}
            extrude(context, id + "F14", {"entities" : qUnion([Q0]), "operationType" : NewBodyOperationType.REMOVE, "oppositeDirection" : true, "depth" : 4.76 * mm, "offsetDistance" : 25.4 * mm});
        }
        {
            var Q0;
            Q0=makeQuery(id+"F14.boolean.opBoolean","COPY",EDGE,{"derivedFrom":makeQuery(id+"F14.opExtrude","SWEPT_EDGE",EDGE,{"disambiguationData":[OSD([sQuery(id+"F13.wireOp",EDGE,"E41.top"),sQuery(id+"F13.wireOp",EDGE,"E41.left")])]})});
            var Q1;
            Q1=makeQuery(id+"F14.boolean.opBoolean","COPY",EDGE,{"derivedFrom":makeQuery(id+"F14.opExtrude","SWEPT_EDGE",EDGE,{"disambiguationData":[OSD([sQuery(id+"F13.wireOp",EDGE,"E41.top"),sQuery(id+"F13.wireOp",EDGE,"E41.right")])]})});
            var Q2;
            Q2=makeQuery(id+"F14.boolean.opBoolean","COPY",EDGE,{"derivedFrom":makeQuery(id+"F14.opExtrude","SWEPT_EDGE",EDGE,{"disambiguationData":[OSD([sQuery(id+"F13.wireOp",EDGE,"E41.bottom"),sQuery(id+"F13.wireOp",EDGE,"E41.right")])]})});
            var Q3;
            Q3=makeQuery(id+"F14.boolean.opBoolean","COPY",EDGE,{"derivedFrom":makeQuery(id+"F14.opExtrude","SWEPT_EDGE",EDGE,{"disambiguationData":[OSD([sQuery(id+"F13.wireOp",EDGE,"E41.bottom"),sQuery(id+"F13.wireOp",EDGE,"E41.left")])]})});
            fillet(context, id + "F15", {"entities" : qUnion([Q0, Q1, Q2, Q3]), "radius" : 3.17 * mm, "tangentPropagation" : true, "allowEdgeOverflow" : false});
        }
        {
            var Q0;
            Q0=makeQuery(id+"F1.opExtrude","SWEPT_EDGE",EDGE,{"disambiguationData":[OSD([sQuery(id+"F0.wireOp",EDGE,"E0.bottom"),sQuery(id+"F0.wireOp",EDGE,"E0.right")])]});
            var Q1;
            Q1=makeQuery(id+"F1.opExtrude","SWEPT_EDGE",EDGE,{"disambiguationData":[OSD([sQuery(id+"F0.wireOp",EDGE,"E0.bottom"),sQuery(id+"F0.wireOp",EDGE,"E0.left")])]});
            var Q2;
            Q2=makeQuery(id+"F1.opExtrude","SWEPT_EDGE",EDGE,{"disambiguationData":[OSD([sQuery(id+"F0.wireOp",EDGE,"E0.top"),sQuery(id+"F0.wireOp",EDGE,"E0.left")])]});
            var Q3;
            Q3=makeQuery(id+"F1.opExtrude","SWEPT_EDGE",EDGE,{"disambiguationData":[OSD([sQuery(id+"F0.wireOp",EDGE,"E0.top"),sQuery(id+"F0.wireOp",EDGE,"E0.right")])]});
            fillet(context, id + "F16", {"entities" : qUnion([Q0, Q1, Q2, Q3]), "radius" : 3.17 * mm, "tangentPropagation" : true, "allowEdgeOverflow" : false});
        }
        {
            var Q0;
            Q0=makeQuery(id+"F1.opExtrude","CAP_FACE",FACE,{"disambiguationData":[OSD([sQuery(id+"F0.wireOp",EDGE,"E0.bottom"),sQuery(id+"F0.wireOp",EDGE,"E0.top"),sQuery(id+"F0.wireOp",EDGE,"E0.left"),sQuery(id+"F0.wireOp",EDGE,"E0.right")])],"isStart":false});
            cPlane(context, id + "F17", {"entities" : qUnion([Q0]), "cplaneType" : CPlaneType.OFFSET, "offset" : 17.46 * mm, "width" : 152.4 * mm, "height" : 152.4 * mm});
        }
        {
            var Q0;
            Q0=qCreatedBy(id+"F17.planeOp",FACE);
            var sketch = newSketch(context, id + "F18", { "sketchPlane" : qUnion([Q0])});
            skLineSegment(sketch, "E42.bottom", {"start": v(190.5, -76.2) * mm, "end": v(-190.5, -76.2) * mm});
            skLineSegment(sketch, "E42.top", {"start": v(190.5, 76.2) * mm, "end": v(-190.5, 76.2) * mm});
            skLineSegment(sketch, "E42.left", {"start": v(190.5, -76.2) * mm, "end": v(190.5, 76.2) * mm});
            skLineSegment(sketch, "E42.right", {"start": v(-190.5, -76.2) * mm, "end": v(-190.5, 76.2) * mm});
            skPoint(sketch, "E42.middle", {"position": v(0, 0) * mm});
            skSolve(sketch);
        }
        {
            var Q0;
            Q0 = qSketchRegion(id + "F18", true);
            extrude(context, id + "F19", {"entities" : qUnion([Q0]), "oppositeDirection" : true, "depth" : 17.46 * mm, "offsetDistance" : 25.4 * mm});
        }
        {
            var Q0;
            Q0=makeQuery(id+"F1.opExtrude","SWEPT_FACE",FACE,{"disambiguationData":[OSD([sQuery(id+"F0.wireOp",EDGE,"E0.bottom")])]});
            var sketch = newSketch(context, id + "F20", { "sketchPlane" : qUnion([Q0])});
            skLineSegment(sketch, "E43.top", {"start": v(38.08, -17.46) * mm, "end": v(0, -17.46) * mm});
            skLineSegment(sketch, "E43.left", {"start": v(38.08, -7.94) * mm, "end": v(38.08, -17.46) * mm});
            skLineSegment(sketch, "E44.bottom", {"start": v(38.08, -7.94) * mm, "end": v(-38.08, -7.94) * mm});
            skLineSegment(sketch, "E44.top", {"start": v(38.08, -26.99) * mm, "end": v(-38.08, -26.99) * mm});
            skLineSegment(sketch, "E44.left", {"start": v(38.08, -7.94) * mm, "end": v(38.08, -26.99) * mm});
            skLineSegment(sketch, "E44.right", {"start": v(-38.08, -7.94) * mm, "end": v(-38.08, -26.99) * mm});
            skPoint(sketch, "E44.middle", {"position": v(0, -17.46) * mm});
            skSolve(sketch);
        }
        {
            var Q0;
            {var subQ1=sQuery(id+"F20.wireOp",EDGE,"E43.top");Q0=makeQuery(id+"F20.imprint","IMPRINT",FACE,{"disambiguationData":[TD([[makeQuery(id+"F20.imprint","IMPRINT",EDGE,{"derivedFrom":subQ1}),-1.0]])]});}
            var Q1;
            {var subQ4=sQuery(id+"F20.wireOp",EDGE,"E43.top");Q1=makeQuery(id+"F20.imprint","IMPRINT",FACE,{"disambiguationData":[TD([[makeQuery(id+"F20.imprint","IMPRINT",EDGE,{"derivedFrom":subQ4}),1.0]])]});}
            extrude(context, id + "F21", {"entities" : qUnion([Q0, Q1]), "operationType" : NewBodyOperationType.REMOVE, "oppositeDirection" : true, "depth" : 6.35 * mm, "offsetDistance" : 25.4 * mm});
        }
        {
            var Q0;
            Q0=makeQuery(id+"F21.boolean.opBoolean","COPY",EDGE,{"derivedFrom":makeQuery(id+"F21.opExtrude","CAP_EDGE",EDGE,{"disambiguationData":[OSD([sQuery(id+"F20.wireOp",EDGE,"E44.bottom")])],"isStart":false})});
            var Q1;
            {var subQ0=sQuery(id+"F20.wireOp",EDGE,"E44.top");var subQ1=sQuery(id+"F20.wireOp",EDGE,"E44.left");var subQ2=sQuery(id+"F20.wireOp",EDGE,"E44.bottom");var subQ3=sQuery(id+"F20.wireOp",EDGE,"E43.left");var subQ6=makeQuery(id+"F21.opExtrude","CAP_EDGE",EDGE,{"disambiguationData":[OSD([subQ3,subQ1])],"isStart":false});Q1=qUnion([makeQuery(id+"F21.boolean.opBoolean","COPY",EDGE,{"disambiguationData":[TD([makeQuery(id+"F21.opExtrude","SWEPT_FACE",FACE,{"disambiguationData":[OSD([subQ2])]})])],"derivedFrom":subQ6}),makeQuery(id+"F21.boolean.opBoolean","COPY",EDGE,{"disambiguationData":[TD([makeQuery(id+"F21.opExtrude","SWEPT_FACE",FACE,{"disambiguationData":[OSD([subQ0])]})])],"derivedFrom":subQ6})]);}
            var Q2;
            Q2=makeQuery(id+"F21.boolean.opBoolean","COPY",EDGE,{"derivedFrom":makeQuery(id+"F21.opExtrude","SWEPT_EDGE",EDGE,{"disambiguationData":[OSD([sQuery(id+"F20.wireOp",EDGE,"E44.bottom"),sQuery(id+"F20.wireOp",EDGE,"E44.right")])]})});
            var Q3;
            Q3=makeQuery(id+"F21.boolean.opBoolean","COPY",EDGE,{"derivedFrom":makeQuery(id+"F21.opExtrude","SWEPT_EDGE",EDGE,{"disambiguationData":[OSD([sQuery(id+"F20.wireOp",EDGE,"E43.left"),sQuery(id+"F20.wireOp",EDGE,"E44.bottom")])]})});
            var Q4;
            {var subQ0=sQuery(id+"F20.wireOp",EDGE,"E44.top");var subQ1=sQuery(id+"F20.wireOp",EDGE,"E44.right");var subQ2=sQuery(id+"F20.wireOp",EDGE,"E44.bottom");var subQ5=makeQuery(id+"F21.opExtrude","CAP_EDGE",EDGE,{"disambiguationData":[OSD([subQ1])],"isStart":false});Q4=qUnion([makeQuery(id+"F21.boolean.opBoolean","COPY",EDGE,{"disambiguationData":[TD([makeQuery(id+"F21.opExtrude","SWEPT_FACE",FACE,{"disambiguationData":[OSD([subQ2])]})])],"derivedFrom":subQ5}),makeQuery(id+"F21.boolean.opBoolean","COPY",EDGE,{"disambiguationData":[TD([makeQuery(id+"F21.opExtrude","SWEPT_FACE",FACE,{"disambiguationData":[OSD([subQ0])]})])],"derivedFrom":subQ5})]);}
            var Q5;
            Q5=makeQuery(id+"F21.boolean.opBoolean","COPY",EDGE,{"derivedFrom":makeQuery(id+"F21.opExtrude","CAP_EDGE",EDGE,{"disambiguationData":[OSD([sQuery(id+"F20.wireOp",EDGE,"E44.top")])],"isStart":false})});
            var Q6;
            Q6=makeQuery(id+"F21.boolean.opBoolean","COPY",EDGE,{"derivedFrom":makeQuery(id+"F21.opExtrude","SWEPT_EDGE",EDGE,{"disambiguationData":[OSD([sQuery(id+"F20.wireOp",EDGE,"E44.top"),sQuery(id+"F20.wireOp",EDGE,"E44.right")])]})});
            var Q7;
            Q7=makeQuery(id+"F21.boolean.opBoolean","COPY",EDGE,{"derivedFrom":makeQuery(id+"F21.opExtrude","SWEPT_EDGE",EDGE,{"disambiguationData":[OSD([sQuery(id+"F20.wireOp",EDGE,"E44.top"),sQuery(id+"F20.wireOp",EDGE,"E44.left")])]})});
            fillet(context, id + "F22", {"entities" : qUnion([Q0, Q1, Q2, Q3, Q4, Q5, Q6, Q7]), "radius" : 6.35 * mm, "tangentPropagation" : true, "allowEdgeOverflow" : false});
        }
        {
            var Q0;
            Q0=makeQuery(id+"F19.opExtrude","SWEPT_EDGE",EDGE,{"disambiguationData":[OSD([sQuery(id+"F18.wireOp",EDGE,"E42.top"),sQuery(id+"F18.wireOp",EDGE,"E42.right")])]});
            var Q1;
            Q1=makeQuery(id+"F19.opExtrude","SWEPT_EDGE",EDGE,{"disambiguationData":[OSD([sQuery(id+"F18.wireOp",EDGE,"E42.top"),sQuery(id+"F18.wireOp",EDGE,"E42.left")])]});
            var Q2;
            Q2=makeQuery(id+"F19.opExtrude","SWEPT_EDGE",EDGE,{"disambiguationData":[OSD([sQuery(id+"F18.wireOp",EDGE,"E42.bottom"),sQuery(id+"F18.wireOp",EDGE,"E42.left")])]});
            var Q3;
            Q3=makeQuery(id+"F19.opExtrude","SWEPT_EDGE",EDGE,{"disambiguationData":[OSD([sQuery(id+"F18.wireOp",EDGE,"E42.bottom"),sQuery(id+"F18.wireOp",EDGE,"E42.right")])]});
            fillet(context, id + "F23", {"entities" : qUnion([Q0, Q1, Q2, Q3]), "radius" : 3.17 * mm, "tangentPropagation" : true, "allowEdgeOverflow" : false});
        }
        {
            var Q0;
            Q0=makeQuery(id+"F19.opExtrude","CAP_FACE",FACE,{"disambiguationData":[OSD([sQuery(id+"F18.wireOp",EDGE,"E42.bottom"),sQuery(id+"F18.wireOp",EDGE,"E42.top"),sQuery(id+"F18.wireOp",EDGE,"E42.left"),sQuery(id+"F18.wireOp",EDGE,"E42.right")])],"isStart":false});
            var sketch = newSketch(context, id + "F24", { "sketchPlane" : qUnion([Q0])});
            skLineSegment(sketch, "E45", {"start": v(0, 0) * mm, "end": v(95.25, 0) * mm});
            skLineSegment(sketch, "E46", {"start": v(0, 0) * mm, "end": v(-95.25, 0) * mm});
            skLineSegment(sketch, "E47.bottom", {"start": v(142.88, -34.93) * mm, "end": v(47.62, -34.93) * mm});
            skLineSegment(sketch, "E47.top", {"start": v(142.88, 34.93) * mm, "end": v(47.62, 34.93) * mm});
            skLineSegment(sketch, "E47.left", {"start": v(142.88, -34.93) * mm, "end": v(142.88, 34.93) * mm});
            skLineSegment(sketch, "E47.right", {"start": v(47.62, -34.93) * mm, "end": v(47.62, 34.93) * mm});
            skPoint(sketch, "E47.middle", {"position": v(95.25, 0) * mm});
            skLineSegment(sketch, "E48.bottom", {"start": v(-69.85, -25.4) * mm, "end": v(-120.65, -25.4) * mm});
            skLineSegment(sketch, "E48.top", {"start": v(-69.85, 25.4) * mm, "end": v(-120.65, 25.4) * mm});
            skLineSegment(sketch, "E48.left", {"start": v(-69.85, -25.4) * mm, "end": v(-69.85, 25.4) * mm});
            skLineSegment(sketch, "E48.right", {"start": v(-120.65, -25.4) * mm, "end": v(-120.65, 25.4) * mm});
            skPoint(sketch, "E48.middle", {"position": v(-95.25, 0) * mm});
            skSolve(sketch);
        }
        {
            var Q0;
            {var subQ3=sQuery(id+"F24.wireOp",EDGE,"E48.bottom");Q0=makeQuery(id+"F24.imprint","IMPRINT",FACE,{"disambiguationData":[TD([[makeQuery(id+"F24.imprint","IMPRINT",EDGE,{"derivedFrom":subQ3}),-1.0]])]});}
            extrude(context, id + "F25", {"entities" : qUnion([Q0]), "operationType" : NewBodyOperationType.REMOVE, "oppositeDirection" : true, "depth" : 9.52 * mm, "offsetDistance" : 25.4 * mm});
        }
        {
            var Q0;
            {var subQ1=sQuery(id+"F24.wireOp",EDGE,"E47.bottom");Q0=makeQuery(id+"F24.imprint","IMPRINT",FACE,{"disambiguationData":[TD([[makeQuery(id+"F24.imprint","IMPRINT",EDGE,{"derivedFrom":subQ1}),-1.0]])]});}
            extrude(context, id + "F26", {"entities" : qUnion([Q0]), "operationType" : NewBodyOperationType.REMOVE, "oppositeDirection" : true, "depth" : 12.7 * mm + 1.59 * mm, "offsetDistance" : 25.4 * mm});
        }
        {
            var Q0;
            Q0=makeQuery(id+"F25.boolean.opBoolean","COPY",EDGE,{"derivedFrom":makeQuery(id+"F25.opExtrude","SWEPT_EDGE",EDGE,{"disambiguationData":[OSD([sQuery(id+"F24.wireOp",EDGE,"E48.top"),sQuery(id+"F24.wireOp",EDGE,"E48.right")])]})});
            var Q1;
            Q1=makeQuery(id+"F26.boolean.opBoolean","COPY",EDGE,{"derivedFrom":makeQuery(id+"F26.opExtrude","SWEPT_EDGE",EDGE,{"disambiguationData":[OSD([sQuery(id+"F24.wireOp",EDGE,"E47.top"),sQuery(id+"F24.wireOp",EDGE,"E47.right")])]})});
            var Q2;
            Q2=makeQuery(id+"F26.boolean.opBoolean","COPY",EDGE,{"derivedFrom":makeQuery(id+"F26.opExtrude","SWEPT_EDGE",EDGE,{"disambiguationData":[OSD([sQuery(id+"F24.wireOp",EDGE,"E47.bottom"),sQuery(id+"F24.wireOp",EDGE,"E47.left")])]})});
            var Q3;
            Q3=makeQuery(id+"F25.boolean.opBoolean","COPY",EDGE,{"derivedFrom":makeQuery(id+"F25.opExtrude","SWEPT_EDGE",EDGE,{"disambiguationData":[OSD([sQuery(id+"F24.wireOp",EDGE,"E48.bottom"),sQuery(id+"F24.wireOp",EDGE,"E48.left")])]})});
            var Q4;
            Q4=makeQuery(id+"F25.boolean.opBoolean","COPY",EDGE,{"derivedFrom":makeQuery(id+"F25.opExtrude","SWEPT_EDGE",EDGE,{"disambiguationData":[OSD([sQuery(id+"F24.wireOp",EDGE,"E48.top"),sQuery(id+"F24.wireOp",EDGE,"E48.left")])]})});
            var Q5;
            Q5=makeQuery(id+"F26.boolean.opBoolean","COPY",EDGE,{"derivedFrom":makeQuery(id+"F26.opExtrude","SWEPT_EDGE",EDGE,{"disambiguationData":[OSD([sQuery(id+"F24.wireOp",EDGE,"E47.top"),sQuery(id+"F24.wireOp",EDGE,"E47.left")])]})});
            var Q6;
            Q6=makeQuery(id+"F25.boolean.opBoolean","COPY",EDGE,{"derivedFrom":makeQuery(id+"F25.opExtrude","SWEPT_EDGE",EDGE,{"disambiguationData":[OSD([sQuery(id+"F24.wireOp",EDGE,"E48.bottom"),sQuery(id+"F24.wireOp",EDGE,"E48.right")])]})});
            var Q7;
            Q7=makeQuery(id+"F26.boolean.opBoolean","COPY",EDGE,{"derivedFrom":makeQuery(id+"F26.opExtrude","SWEPT_EDGE",EDGE,{"disambiguationData":[OSD([sQuery(id+"F24.wireOp",EDGE,"E47.bottom"),sQuery(id+"F24.wireOp",EDGE,"E47.right")])]})});
            fillet(context, id + "F27", {"entities" : qUnion([Q0, Q1, Q2, Q3, Q4, Q5, Q6, Q7]), "radius" : 3.17 * mm, "tangentPropagation" : true, "allowEdgeOverflow" : false});
        }
        {
            var Q0;
            Q0=makeQuery(id+"F19.opExtrude","CAP_FACE",FACE,{"disambiguationData":[OSD([sQuery(id+"F18.wireOp",EDGE,"E42.bottom"),sQuery(id+"F18.wireOp",EDGE,"E42.top"),sQuery(id+"F18.wireOp",EDGE,"E42.left"),sQuery(id+"F18.wireOp",EDGE,"E42.right")])],"isStart":false});
            var sketch = newSketch(context, id + "F28", { "sketchPlane" : qUnion([Q0])});
            skLineSegment(sketch, "E49.bottom", {"start": v(-190.5, -76.2) * mm, "end": v(-171.45, -76.2) * mm});
            skLineSegment(sketch, "E49.top", {"start": v(-190.5, -57.15) * mm, "end": v(-171.45, -57.15) * mm});
            skLineSegment(sketch, "E49.left", {"start": v(-190.5, -76.2) * mm, "end": v(-190.5, -57.15) * mm});
            skLineSegment(sketch, "E49.right", {"start": v(-171.45, -76.2) * mm, "end": v(-171.45, -57.15) * mm});
            skLineSegment(sketch, "E50.bottom", {"start": v(190.5, -76.2) * mm, "end": v(171.45, -76.2) * mm});
            skLineSegment(sketch, "E50.top", {"start": v(190.5, -57.15) * mm, "end": v(171.45, -57.15) * mm});
            skLineSegment(sketch, "E50.left", {"start": v(190.5, -76.2) * mm, "end": v(190.5, -57.15) * mm});
            skLineSegment(sketch, "E50.right", {"start": v(171.45, -76.2) * mm, "end": v(171.45, -57.15) * mm});
            skCircle(sketch, "E51", {"center": v(171.45, -57.15) * mm, "radius": 4 * mm});
            skCircle(sketch, "E52", {"center": v(-171.45, -57.15) * mm, "radius": 4 * mm});
            skSolve(sketch);
        }
        {
            var Q0;
            {var subQ0=sQuery(id+"F28.wireOp",EDGE,"E50.right");var subQ1=sQuery(id+"F28.wireOp",EDGE,"E50.top");var subQ2=makeQuery(id+"F28.imprint","INTERSECT",VERTEX,{"derivedFrom":[subQ1,subQ0]});Q0=makeQuery(id+"F28.imprint","IMPRINT",FACE,{"disambiguationData":[TD([[makeQuery(id+"F28.imprint","IMPRINT",EDGE,{"disambiguationData":[TD([[subQ2,1.0]])],"derivedFrom":subQ1}),-1.0]])]});}
            var Q1;
            {var subQ0=sQuery(id+"F28.wireOp",EDGE,"E50.right");var subQ1=sQuery(id+"F28.wireOp",EDGE,"E50.top");var subQ2=makeQuery(id+"F28.imprint","INTERSECT",VERTEX,{"derivedFrom":[subQ1,subQ0]});Q1=makeQuery(id+"F28.imprint","IMPRINT",FACE,{"disambiguationData":[TD([[makeQuery(id+"F28.imprint","IMPRINT",EDGE,{"disambiguationData":[TD([[subQ2,1.0]])],"derivedFrom":subQ1}),1.0]])]});}
            var Q2;
            {var subQ0=sQuery(id+"F28.wireOp",EDGE,"E49.right");var subQ1=sQuery(id+"F28.wireOp",EDGE,"E49.top");var subQ2=makeQuery(id+"F28.imprint","INTERSECT",VERTEX,{"derivedFrom":[subQ1,subQ0]});Q2=makeQuery(id+"F28.imprint","IMPRINT",FACE,{"disambiguationData":[TD([[makeQuery(id+"F28.imprint","IMPRINT",EDGE,{"disambiguationData":[TD([[subQ2,1.0]])],"derivedFrom":subQ1}),1.0]])]});}
            var Q3;
            {var subQ0=sQuery(id+"F28.wireOp",EDGE,"E49.right");var subQ1=sQuery(id+"F28.wireOp",EDGE,"E49.top");var subQ2=makeQuery(id+"F28.imprint","INTERSECT",VERTEX,{"derivedFrom":[subQ1,subQ0]});Q3=makeQuery(id+"F28.imprint","IMPRINT",FACE,{"disambiguationData":[TD([[makeQuery(id+"F28.imprint","IMPRINT",EDGE,{"disambiguationData":[TD([[subQ2,1.0]])],"derivedFrom":subQ1}),-1.0]])]});}
            var Q4;
            Q4=sQuery(id+"F28.wireOp",EDGE,"E52");
            var Q5;
            Q5=sQuery(id+"F28.wireOp",EDGE,"E51");
            extrude(context, id + "F29", {"entities" : qUnion([Q0, Q1, Q2, Q3]), "operationType" : NewBodyOperationType.REMOVE, "surfaceEntities" : qUnion([Q4, Q5]), "oppositeDirection" : true, "depth" : 4.5 * mm, "offsetDistance" : 25.4 * mm});
        }
        {
            var Q0;
            Q0=makeQuery(id+"F19.opExtrude","CAP_FACE",FACE,{"disambiguationData":[OSD([sQuery(id+"F18.wireOp",EDGE,"E42.bottom"),sQuery(id+"F18.wireOp",EDGE,"E42.top"),sQuery(id+"F18.wireOp",EDGE,"E42.left"),sQuery(id+"F18.wireOp",EDGE,"E42.right")])],"isStart":false});
            var sketch = newSketch(context, id + "F30", { "sketchPlane" : qUnion([Q0])});
            skCircle(sketch, "E53", {"center": v(171.45, 69.5) * mm, "radius": 5 * mm});
            skCircle(sketch, "E54", {"center": v(-171.45, 69.5) * mm, "radius": 5 * mm});
            skSolve(sketch);
        }
        {
            var Q0;
            Q0=makeQuery(id+"F30.imprint","IMPRINT",FACE,{"disambiguationData":[TD([[makeQuery(id+"F30.imprint","IMPRINT",EDGE,{"derivedFrom":sQuery(id+"F30.wireOp",EDGE,"E54")}),1.0]])]});
            var Q1;
            Q1=makeQuery(id+"F30.imprint","IMPRINT",FACE,{"disambiguationData":[TD([[makeQuery(id+"F30.imprint","IMPRINT",EDGE,{"derivedFrom":sQuery(id+"F30.wireOp",EDGE,"E53")}),1.0]])]});
            extrude(context, id + "F31", {"entities" : qUnion([Q0, Q1]), "operationType" : NewBodyOperationType.REMOVE, "oppositeDirection" : true, "depth" : 11.5 * mm, "offsetDistance" : 25.4 * mm});
        }
        {
            var Q0;
            Q0=makeQuery(id+"F1.opExtrude","CAP_FACE",FACE,{"disambiguationData":[OSD([sQuery(id+"F0.wireOp",EDGE,"E0.bottom"),sQuery(id+"F0.wireOp",EDGE,"E0.top"),sQuery(id+"F0.wireOp",EDGE,"E0.left"),sQuery(id+"F0.wireOp",EDGE,"E0.right")])],"isStart":true});
            var sketch = newSketch(context, id + "F32", { "sketchPlane" : qUnion([Q0])});
            skCircle(sketch, "E55", {"center": v(-166.62, 46.99) * mm, "radius": 4.76 * mm});
            skCircle(sketch, "E56", {"center": v(-166.62, 46.99) * mm, "radius": 2.38 * mm});
            skSolve(sketch);
        }
        {
            var Q0;
            Q0=makeQuery(id+"F32.imprint","IMPRINT",FACE,{"disambiguationData":[TD([[makeQuery(id+"F32.imprint","IMPRINT",EDGE,{"derivedFrom":sQuery(id+"F32.wireOp",EDGE,"E55")}),1.0]])]});
            extrude(context, id + "F33", {"entities" : qUnion([Q0]), "depth" : -9.52 * mm, "offsetDistance" : 25.4 * mm});
        }
        {
            var Q0;
            Q0=makeQuery(id+"F32.imprint","IMPRINT",FACE,{"disambiguationData":[TD([[makeQuery(id+"F32.imprint","IMPRINT",EDGE,{"derivedFrom":sQuery(id+"F32.wireOp",EDGE,"E56")}),1.0]])]});
            var Q1;
            Q1=makeQuery(id+"F32.imprint","IMPRINT",FACE,{"disambiguationData":[TD([[makeQuery(id+"F32.imprint","IMPRINT",EDGE,{"derivedFrom":sQuery(id+"F32.wireOp",EDGE,"E55")}),1.0]])]});
            extrude(context, id + "F34", {"entities" : qUnion([Q0, Q1]), "operationType" : NewBodyOperationType.REMOVE, "oppositeDirection" : true, "depth" : 9.52 * mm, "offsetDistance" : 25.4 * mm});
        }
        {
            var Q0;
            {var subQ0=sQuery(id+"F32.wireOp",EDGE,"E55");var subQ1=sQuery(id+"F32.wireOp",EDGE,"rNdfeVHo-Q0o1-b4VG-QCh5-1CthINOZI3VE");var subQ2=makeQuery(id+"F32.imprint","INTERSECT",VERTEX,{"derivedFrom":[subQ1,subQ0]});Q0=makeQuery(id+"F32.imprint","IMPRINT",FACE,{"disambiguationData":[TD([[makeQuery(id+"F32.imprint","IMPRINT",EDGE,{"disambiguationData":[TD([[subQ2,-1.0]])],"derivedFrom":subQ1}),1.0]])]});}
            var Q1;
            {var subQ0=sQuery(id+"F32.wireOp",EDGE,"E55");var subQ1=sQuery(id+"F32.wireOp",EDGE,"rNdfeVHo-Q0o1-b4VG-QCh5-1CthINOZI3VE");var subQ2=makeQuery(id+"F32.imprint","INTERSECT",VERTEX,{"derivedFrom":[subQ1,subQ0]});Q1=makeQuery(id+"F32.imprint","IMPRINT",FACE,{"disambiguationData":[TD([[makeQuery(id+"F32.imprint","IMPRINT",EDGE,{"disambiguationData":[TD([[subQ2,-1.0]])],"derivedFrom":subQ1}),-1.0]])]});}
            var Q2;
            Q2=makeQuery(id+"F32.imprint","IMPRINT",FACE,{"disambiguationData":[TD([[makeQuery(id+"F32.imprint","IMPRINT",EDGE,{"derivedFrom":sQuery(id+"F32.wireOp",EDGE,"E55")}),1.0]])]});
            extrude(context, id + "F35", {"entities" : qUnion([Q0, Q1, Q2]), "operationType" : NewBodyOperationType.ADD, "depth" : 1.59 * mm, "offsetDistance" : 25.4 * mm});
        }
        {
            var Q0;
            Q0=makeQuery(id+"F35.opExtrude","CAP_EDGE",EDGE,{"disambiguationData":[OSD([sQuery(id+"F32.wireOp",EDGE,"E55")])],"isStart":false});
            chamfer(context, id + "F36", {"entities" : qUnion([Q0]), "width" : 1.59 * mm, "tangentPropagation" : true});
        }
        {
            var Q0;
            Q0=makeQuery(id+"F1.opExtrude","CAP_EDGE",EDGE,{"disambiguationData":[OSD([sQuery(id+"F0.wireOp",EDGE,"E0.right")])],"isStart":true});
            fillet(context, id + "F37", {"entities" : qUnion([Q0]), "radius" : 3.17 * mm, "tangentPropagation" : true, "allowEdgeOverflow" : false});
        }
    });
